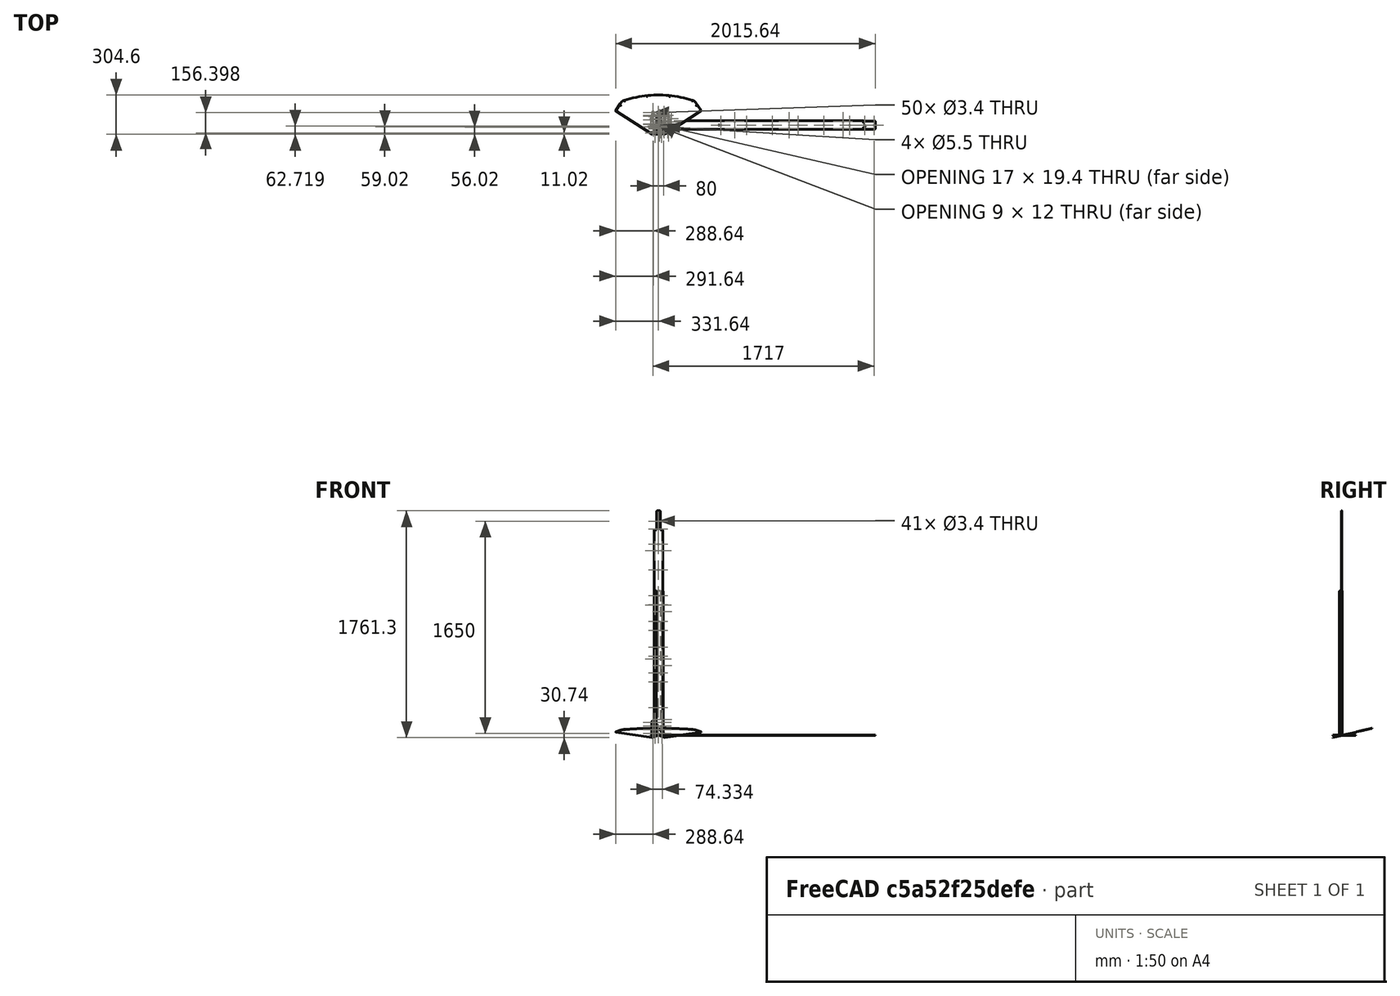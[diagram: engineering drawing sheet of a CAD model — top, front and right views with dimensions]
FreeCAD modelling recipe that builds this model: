
FCSTD DOCUMENT  (FreeCAD 0.21R32532 (Git))
Label: compostit_full_size2part_ss
License: All rights reserved
LicenseURL: http://en.wikipedia.org/wiki/All_rights_reserved
objects: TechDraw::DrawViewDimension×59, Sketcher::SketchObject×27, TechDraw::DrawViewPart×26, TechDraw::DrawPage×11, App::Link×9, Part::Feature×9, App::DocumentObjectGroup×8, Part::Mirroring×3, PartDesign::FeatureBase×1, PartDesign::Body×1, TechDraw::DrawSVGTemplate×1
note: 150 computed .brp shape members not serialized (recipe doc carries the construction recipe); baked Part::Feature solids carry a one-line shape summary decoded from their .brp
EXTERNAL_REF file=composit_full_size2part.FCStd obj=Body029
EXTERNAL_REF file=composit_full_size2part.FCStd obj=Body033
EXTERNAL_REF file=composit_full_size2part.FCStd obj=Body034
EXTERNAL_REF file=composit_full_size2part.FCStd obj=Body058
EXTERNAL_REF file=composit_full_size2part.FCStd obj=cover_bended
EXTERNAL_REF file=composit_full_size2part.FCStd obj=Body065
EXTERNAL_REF file=composit_full_size2part.FCStd obj=Body064
EXTERNAL_REF file=composit_full_size2part.FCStd obj=Body066
EXTERNAL_REF file=composit_full_size2part.FCStd obj=Body067

FEATURE [App::Link] Link  label="pillar"
  LinkedObject = -> <external composit_full_size2part.FCStd>#Body029
  expr: LinkedObject = composit_full_size2part#<<pillar_material_0.45ansi>>._self
FEATURE [App::Link] Link001
  LinkedObject = -> <external composit_full_size2part.FCStd>#Body033
  expr: LinkedObject = composit_full_size2part#<<pillar_corner_top_material_0.40ansi>>._self
FEATURE [App::Link] Link002
  LinkedObject = -> <external composit_full_size2part.FCStd>#Body034
  expr: LinkedObject = composit_full_size2part#<<pillar_corner_bottom_material_0.40ansi>>._self
FEATURE [App::Link] Link003  label="dec_corner_link"
  LinkedObject = -> <external composit_full_size2part.FCStd>#Body058
  expr: LinkedObject = composit_full_size2part#<<dec_corner_material_0.50ansi>>._self
FEATURE [App::Link] Link004
  LinkedObject = -> <external composit_full_size2part.FCStd>#cover_bended
  expr: LinkedObject = composit_full_size2part#<<cover_bended_material_0.45ansi>>._self
FEATURE [Part::Feature] Unfold001
  shape: bbox 28.6 x 144.4 x 2.247 mm, 22 faces (baked)
FEATURE [Sketcher::SketchObject] Unfold_Sketch001
  FullyConstrained = false
  sketch-geometry (20):
    g0: BSplineCurve PolesCount=34 KnotsCount=9 Degree=5 IsPeriodic=0
    g1: LineSegment StartX=-9.3 StartY=74.3982 StartZ=0 EndX=9.3 EndY=74.3982 EndZ=0
    g2: BSplineCurve PolesCount=34 KnotsCount=9 Degree=5 IsPeriodic=0
    g3: LineSegment StartX=-9.3 StartY=-70 StartZ=0 EndX=9.3 EndY=-70 EndZ=0
    g4: BSplineCurve PolesCount=34 KnotsCount=9 Degree=5 IsPeriodic=0
    g5: BSplineCurve PolesCount=34 KnotsCount=9 Degree=5 IsPeriodic=0
    g6: ArcOfCircle CenterX=-3 CenterY=-19.5 CenterZ=0 NormalX=0 NormalY=0 NormalZ=1 AngleXU=0 Radius=1.5 StartAngle=3.14159 EndAngle=4.71239
    g7: LineSegment StartX=-4.5 StartY=-19.5 StartZ=0 EndX=-4.5 EndY=-10.5 EndZ=0
    g8: ArcOfCircle CenterX=-3 CenterY=-10.5 CenterZ=0 NormalX=0 NormalY=0 NormalZ=1 AngleXU=0 Radius=1.5 StartAngle=1.5708 EndAngle=3.14159
    g9: LineSegment StartX=-3 StartY=-9 StartZ=0 EndX=3 EndY=-9 EndZ=0
    g10: ArcOfCircle CenterX=3 CenterY=-10.5 CenterZ=0 NormalX=0 NormalY=0 NormalZ=1 AngleXU=0 Radius=1.5 StartAngle=-1.91e-13 EndAngle=1.5708
    g11: LineSegment StartX=4.5 StartY=-10.5 StartZ=0 EndX=4.5 EndY=-19.5 EndZ=0
    g12: ArcOfCircle CenterX=3 CenterY=-19.5 CenterZ=0 NormalX=0 NormalY=0 NormalZ=1 AngleXU=0 Radius=1.5 StartAngle=4.71239 EndAngle=6.28319
    g13: LineSegment StartX=3 StartY=-21 StartZ=0 EndX=-3 EndY=-21 EndZ=0
    g14: Circle CenterX=3.46e-14 CenterY=66.3982 CenterZ=0 NormalX=0 NormalY=0 NormalZ=1 AngleXU=-5e-16 Radius=1.7
    g15: Circle CenterX=6e-16 CenterY=-60 CenterZ=0 NormalX=0 NormalY=0 NormalZ=1 AngleXU=-3.14159 Radius=1.7
    g16: Circle CenterX=4.6e-15 CenterY=6.39823 CenterZ=0 NormalX=0 NormalY=0 NormalZ=1 AngleXU=-5e-16 Radius=1.7
    g17: Circle CenterX=6e-16 CenterY=-30 CenterZ=0 NormalX=0 NormalY=0 NormalZ=1 AngleXU=-3.14159 Radius=1.7
    g18: LineSegment StartX=-14.3 StartY=69.3982 StartZ=0 EndX=-14.3 EndY=-65 EndZ=0
    g19: LineSegment StartX=14.3 StartY=69.3982 StartZ=0 EndX=14.3 EndY=-65 EndZ=0
FEATURE [Sketcher::SketchObject] Unfold_Sketch_Outline001
  FullyConstrained = false
  sketch-geometry (8):
    g0: BSplineCurve PolesCount=34 KnotsCount=9 Degree=5 IsPeriodic=0
    g1: LineSegment StartX=-9.3 StartY=74.3982 StartZ=0 EndX=9.3 EndY=74.3982 EndZ=0
    g2: BSplineCurve PolesCount=34 KnotsCount=9 Degree=5 IsPeriodic=0
    g3: LineSegment StartX=-14.3 StartY=69.3982 StartZ=0 EndX=-14.3 EndY=-65 EndZ=0
    g4: BSplineCurve PolesCount=34 KnotsCount=9 Degree=5 IsPeriodic=0
    g5: LineSegment StartX=-9.3 StartY=-70 StartZ=0 EndX=9.3 EndY=-70 EndZ=0
    g6: BSplineCurve PolesCount=34 KnotsCount=9 Degree=5 IsPeriodic=0
    g7: LineSegment StartX=14.3 StartY=69.3982 StartZ=0 EndX=14.3 EndY=-65 EndZ=0
FEATURE [Sketcher::SketchObject] Unfold_Sketch_Internal
  FullyConstrained = false
  sketch-geometry (12):
    g0: ArcOfCircle CenterX=-3 CenterY=-19.5 CenterZ=0 NormalX=0 NormalY=0 NormalZ=1 AngleXU=0 Radius=1.5 StartAngle=3.14159 EndAngle=4.71239
    g1: LineSegment StartX=3 StartY=-21 StartZ=0 EndX=-3 EndY=-21 EndZ=0
    g2: ArcOfCircle CenterX=3 CenterY=-19.5 CenterZ=0 NormalX=0 NormalY=0 NormalZ=1 AngleXU=0 Radius=1.5 StartAngle=4.71239 EndAngle=6.28319
    g3: LineSegment StartX=4.5 StartY=-10.5 StartZ=0 EndX=4.5 EndY=-19.5 EndZ=0
    g4: ArcOfCircle CenterX=3 CenterY=-10.5 CenterZ=0 NormalX=0 NormalY=0 NormalZ=1 AngleXU=0 Radius=1.5 StartAngle=-1.91e-13 EndAngle=1.5708
    g5: LineSegment StartX=-3 StartY=-9 StartZ=0 EndX=3 EndY=-9 EndZ=0
    g6: ArcOfCircle CenterX=-3 CenterY=-10.5 CenterZ=0 NormalX=0 NormalY=0 NormalZ=1 AngleXU=0 Radius=1.5 StartAngle=1.5708 EndAngle=3.14159
    g7: LineSegment StartX=-4.5 StartY=-19.5 StartZ=0 EndX=-4.5 EndY=-10.5 EndZ=0
    g8: Circle CenterX=6e-16 CenterY=-60 CenterZ=0 NormalX=0 NormalY=0 NormalZ=1 AngleXU=-3.14159 Radius=1.7
    g9: Circle CenterX=3.46e-14 CenterY=66.3982 CenterZ=0 NormalX=0 NormalY=0 NormalZ=1 AngleXU=-5e-16 Radius=1.7
    g10: Circle CenterX=4.6e-15 CenterY=6.39823 CenterZ=0 NormalX=0 NormalY=0 NormalZ=1 AngleXU=-5e-16 Radius=1.7
    g11: Circle CenterX=6e-16 CenterY=-30 CenterZ=0 NormalX=0 NormalY=0 NormalZ=1 AngleXU=-3.14159 Radius=1.7
FEATURE [Sketcher::SketchObject] Unfold_Sketch_bends001
  FullyConstrained = false
  Placement = pos=(0,-0.25401,0.626835) rot=(1,0,0;0.385004rad)
  sketch-geometry (1):
    g0: LineSegment StartX=14.3 StartY=-1.66905 StartZ=0 EndX=-14.3 EndY=-1.66905 EndZ=0
FEATURE [Part::Feature] Unfold002
  Placement = pos=(0,0,0) rot=(1,0,0;0.115926rad)
  shape: bbox 663.3 x 304.6 x 72.37 mm, 42 faces (baked)
  expr: .Placement.Rotation.Angle = -<<composit_full_size2part>>#<<bend_angle_sketch>>.Constraints.angle
FEATURE [Sketcher::SketchObject] Unfold_Sketch002
  FullyConstrained = false
  sketch-geometry (47):
    g0: ArcOfCircle CenterX=1.08768 CenterY=-0.0209948 CenterZ=0 NormalX=0 NormalY=0 NormalZ=1 AngleXU=-1.5708 Radius=6 StartAngle=2.93378 EndAngle=3.41126
    g1: LineSegment StartX=-0.510793 StartY=5.76216 StartZ=0 EndX=-13.5644 EndY=14.402 EndZ=0
    g2: ArcOfCircle CenterX=-15.8107 CenterY=11.0082 CenterZ=0 NormalX=0 NormalY=0 NormalZ=1 AngleXU=0.986118 Radius=4.06986 StartAngle=-9e-16 EndAngle=1.0472
    g3: ArcOfCircle CenterX=-19.4427 CenterY=18.2927 CenterZ=0 NormalX=0 NormalY=0 NormalZ=1 AngleXU=0.986118 Radius=4.06986 StartAngle=3.30821 EndAngle=4.18879
    g4: LineSegment StartX=-21.095 StartY=14.5734 StartZ=0 EndX=-72.4671 EndY=48.5753 EndZ=0
    g5: ArcOfCircle CenterX=-71.8547 CenterY=49.3658 CenterZ=0 NormalX=0 NormalY=0 NormalZ=1 AngleXU=0.986118 Radius=1 StartAngle=1.5708 EndAngle=3.06709
    g6: LineSegment StartX=-72.6886 StartY=49.9178 StartZ=0 EndX=113.036 EndY=330.522 EndZ=0
    g7: ArcOfCircle CenterX=115.121 CenterY=329.142 CenterZ=0 NormalX=0 NormalY=0 NormalZ=1 AngleXU=0.986118 Radius=2.5 StartAngle=0 EndAngle=1.5708
    g8: LineSegment StartX=116.501 StartY=331.227 StartZ=0 EndX=170.6 EndY=295.42 EndZ=0
    g9: BSplineCurve PolesCount=15 KnotsCount=13 Degree=3 IsPeriodic=0
    g10: BSplineCurve PolesCount=15 KnotsCount=13 Degree=3 IsPeriodic=0
    g11: BSplineCurve PolesCount=15 KnotsCount=13 Degree=3 IsPeriodic=0
    g12: ArcOfCircle CenterX=1.05156 CenterY=-5.68e-14 CenterZ=0 NormalX=0 NormalY=0 NormalZ=1 AngleXU=-1.5708 Radius=6 StartAngle=0.845226 EndAngle=2.29637
    g13: BSplineCurve PolesCount=15 KnotsCount=13 Degree=3 IsPeriodic=0
    g14: BSplineCurve PolesCount=15 KnotsCount=13 Degree=3 IsPeriodic=0
    g15: BSplineCurve PolesCount=15 KnotsCount=13 Degree=3 IsPeriodic=0
    g16: ArcOfCircle CenterX=174.836 CenterY=292.289 CenterZ=0 NormalX=0 NormalY=0 NormalZ=1 AngleXU=1.5708 Radius=1.5 StartAngle=5.72892 EndAngle=6.93163
    g17: ArcOfCircle CenterX=146.678 CenterY=246.798 CenterZ=0 NormalX=0 NormalY=0 NormalZ=1 AngleXU=-1.5708 Radius=55 StartAngle=1.87889 EndAngle=2.58733
    g18: ArcOfCircle CenterX=-628.863 CenterY=0 CenterZ=0 NormalX=0 NormalY=0 NormalZ=1 AngleXU=-1.5708 Radius=868.863 StartAngle=1.2627 EndAngle=1.87889
    g19: ArcOfCircle CenterX=146.678 CenterY=-246.798 CenterZ=0 NormalX=0 NormalY=0 NormalZ=1 AngleXU=-1.5708 Radius=55 StartAngle=0.554262 EndAngle=1.2627
    g20: ArcOfCircle CenterX=174.836 CenterY=-292.289 CenterZ=0 NormalX=0 NormalY=0 NormalZ=1 AngleXU=-1.5708 Radius=1.5 StartAngle=5.63474 EndAngle=6.83745
    g21: LineSegment StartX=116.501 StartY=-331.227 StartZ=0 EndX=170.6 EndY=-295.42 EndZ=0
    g22: ArcOfCircle CenterX=115.121 CenterY=-329.142 CenterZ=0 NormalX=0 NormalY=0 NormalZ=1 AngleXU=-0.986118 Radius=2.5 StartAngle=4.71239 EndAngle=6.28319
    g23: LineSegment StartX=-72.6886 StartY=-49.9178 StartZ=0 EndX=113.036 EndY=-330.522 EndZ=0
    g24: ArcOfCircle CenterX=-71.8547 CenterY=-49.3658 CenterZ=0 NormalX=0 NormalY=0 NormalZ=1 AngleXU=-0.986118 Radius=1 StartAngle=3.21609 EndAngle=4.71239
    g25: LineSegment StartX=-21.095 StartY=-14.5734 StartZ=0 EndX=-72.4671 EndY=-48.5753 EndZ=0
    g26: LineSegment StartX=-0.510793 StartY=-5.76216 StartZ=0 EndX=-13.5644 EndY=-14.402 EndZ=0
    g27: ArcOfCircle CenterX=-15.8107 CenterY=-11.0082 CenterZ=0 NormalX=0 NormalY=0 NormalZ=1 AngleXU=-0.986118 Radius=4.06986 StartAngle=5.23599 EndAngle=6.28319
    g28: ArcOfCircle CenterX=-19.4427 CenterY=-18.2927 CenterZ=0 NormalX=0 NormalY=0 NormalZ=1 AngleXU=-0.986118 Radius=4.06986 StartAngle=2.0944 EndAngle=2.97497
    g29: Circle CenterX=228.876 CenterY=-88.304 CenterZ=0 NormalX=0 NormalY=0 NormalZ=1 AngleXU=-1.5708 Radius=1.7
    g30: Circle CenterX=228.876 CenterY=88.304 CenterZ=0 NormalX=0 NormalY=0 NormalZ=1 AngleXU=1.5708 Radius=1.7
    g31: Circle CenterX=-60.5239 CenterY=57.4259 CenterZ=0 NormalX=0 NormalY=0 NormalZ=1 AngleXU=0.986118 Radius=1.7
    g32: Circle CenterX=-60.5239 CenterY=-57.4259 CenterZ=0 NormalX=0 NormalY=0 NormalZ=1 AngleXU=-0.986118 Radius=1.7
    g33: Circle CenterX=-18.8294 CenterY=29.8293 CenterZ=0 NormalX=0 NormalY=0 NormalZ=1 AngleXU=0.986118 Radius=1.7
    g34: Circle CenterX=-18.8294 CenterY=-29.8293 CenterZ=0 NormalX=0 NormalY=0 NormalZ=1 AngleXU=-0.986118 Radius=1.7
    g35: Circle CenterX=156.271 CenterY=294.381 CenterZ=0 NormalX=0 NormalY=0 NormalZ=1 AngleXU=0.986118 Radius=1.7
    g36: Circle CenterX=193.31 CenterY=-261.294 CenterZ=0 NormalX=0 NormalY=0 NormalZ=1 AngleXU=-1.5708 Radius=1.7
    g37: Circle CenterX=193.31 CenterY=261.294 CenterZ=0 NormalX=0 NormalY=0 NormalZ=1 AngleXU=1.5708 Radius=1.7
    g38: Circle CenterX=156.271 CenterY=-294.381 CenterZ=0 NormalX=0 NormalY=0 NormalZ=1 AngleXU=-0.986118 Radius=1.7
    g39: Circle CenterX=114.576 CenterY=321.977 CenterZ=0 NormalX=0 NormalY=0 NormalZ=1 AngleXU=0.986118 Radius=1.7
    g40: Circle CenterX=114.576 CenterY=-321.977 CenterZ=0 NormalX=0 NormalY=0 NormalZ=1 AngleXU=-0.986118 Radius=1.7
    g41: ArcOfCircle CenterX=1.08768 CenterY=0.0209948 CenterZ=0 NormalX=0 NormalY=0 NormalZ=1 AngleXU=-1.5708 Radius=6 StartAngle=0 EndAngle=0.207814
    g42: ArcOfCircle CenterX=1.08768 CenterY=0.0209948 CenterZ=0 NormalX=0 NormalY=0 NormalZ=1 AngleXU=-1.5708 Radius=6 StartAngle=6.01352 EndAngle=6.28319
    g43: LineSegment StartX=173.93 StartY=-293.484 StartZ=0 EndX=170.6 EndY=-295.42 EndZ=0
    g44: LineSegment StartX=170.6 StartY=295.42 StartZ=0 EndX=173.93 EndY=293.484 EndZ=0
    g45: LineSegment StartX=115.121 StartY=-331.642 StartZ=0 EndX=121.023 EndY=-331.642 EndZ=0
    g46: LineSegment StartX=115.121 StartY=-331.642 StartZ=0 EndX=115.121 EndY=331.592 EndZ=0
  constraints (6):
    c: Block(g7)
    c: Block(g22)
    c: Horizontal(g45)
    c: Tangent(g45,g22) = -1.5708
    c: Vertical(g46)
    c: Distance(g46) = 663.233
FEATURE [Sketcher::SketchObject] Unfold_Sketch_Outline002
  FullyConstrained = false
  sketch-geometry (33):
    g0: BSplineCurve PolesCount=15 KnotsCount=13 Degree=3 IsPeriodic=0
    g1: BSplineCurve PolesCount=15 KnotsCount=13 Degree=3 IsPeriodic=0
    g2: ArcOfCircle CenterX=1.08768 CenterY=-0.0209948 CenterZ=0 NormalX=0 NormalY=0 NormalZ=1 AngleXU=-1.5708 Radius=6 StartAngle=2.93378 EndAngle=3.41126
    g3: LineSegment StartX=-0.510793 StartY=5.76216 StartZ=0 EndX=-13.5644 EndY=14.402 EndZ=0
    g4: ArcOfCircle CenterX=-15.8107 CenterY=11.0082 CenterZ=0 NormalX=0 NormalY=0 NormalZ=1 AngleXU=0.986118 Radius=4.06986 StartAngle=-9e-16 EndAngle=1.0472
    g5: ArcOfCircle CenterX=-19.4427 CenterY=18.2927 CenterZ=0 NormalX=0 NormalY=0 NormalZ=1 AngleXU=0.986118 Radius=4.06986 StartAngle=3.30821 EndAngle=4.18879
    g6: LineSegment StartX=-21.095 StartY=14.5734 StartZ=0 EndX=-72.4671 EndY=48.5753 EndZ=0
    g7: ArcOfCircle CenterX=-71.8547 CenterY=49.3658 CenterZ=0 NormalX=0 NormalY=0 NormalZ=1 AngleXU=0.986118 Radius=1 StartAngle=1.5708 EndAngle=3.06709
    g8: LineSegment StartX=-72.6886 StartY=49.9178 StartZ=0 EndX=113.036 EndY=330.522 EndZ=0
    g9: ArcOfCircle CenterX=115.121 CenterY=329.142 CenterZ=0 NormalX=0 NormalY=0 NormalZ=1 AngleXU=0.986118 Radius=2.5 StartAngle=0 EndAngle=1.5708
    g10: LineSegment StartX=116.501 StartY=331.227 StartZ=0 EndX=170.6 EndY=295.42 EndZ=0
    g11: LineSegment StartX=170.6 StartY=295.42 StartZ=0 EndX=173.93 EndY=293.484 EndZ=0
    g12: ArcOfCircle CenterX=174.836 CenterY=292.289 CenterZ=0 NormalX=0 NormalY=0 NormalZ=1 AngleXU=1.5708 Radius=1.5 StartAngle=5.72892 EndAngle=6.93163
    g13: ArcOfCircle CenterX=146.678 CenterY=246.798 CenterZ=0 NormalX=0 NormalY=0 NormalZ=1 AngleXU=-1.5708 Radius=55 StartAngle=1.87889 EndAngle=2.58733
    g14: ArcOfCircle CenterX=-628.863 CenterY=0 CenterZ=0 NormalX=0 NormalY=0 NormalZ=1 AngleXU=-1.5708 Radius=868.863 StartAngle=1.2627 EndAngle=1.87889
    g15: ArcOfCircle CenterX=146.678 CenterY=-246.798 CenterZ=0 NormalX=0 NormalY=0 NormalZ=1 AngleXU=-1.5708 Radius=55 StartAngle=0.554262 EndAngle=1.2627
    g16: ArcOfCircle CenterX=174.836 CenterY=-292.289 CenterZ=0 NormalX=0 NormalY=0 NormalZ=1 AngleXU=-1.5708 Radius=1.5 StartAngle=5.63474 EndAngle=6.83745
    g17: LineSegment StartX=173.93 StartY=-293.484 StartZ=0 EndX=170.6 EndY=-295.42 EndZ=0
    g18: LineSegment StartX=116.501 StartY=-331.227 StartZ=0 EndX=170.6 EndY=-295.42 EndZ=0
    g19: ArcOfCircle CenterX=115.121 CenterY=-329.142 CenterZ=0 NormalX=0 NormalY=0 NormalZ=1 AngleXU=-0.986118 Radius=2.5 StartAngle=4.71239 EndAngle=6.28319
    g20: LineSegment StartX=-72.6886 StartY=-49.9178 StartZ=0 EndX=113.036 EndY=-330.522 EndZ=0
    g21: ArcOfCircle CenterX=-71.8547 CenterY=-49.3658 CenterZ=0 NormalX=0 NormalY=0 NormalZ=1 AngleXU=-0.986118 Radius=1 StartAngle=3.21609 EndAngle=4.71239
    g22: LineSegment StartX=-21.095 StartY=-14.5734 StartZ=0 EndX=-72.4671 EndY=-48.5753 EndZ=0
    g23: ArcOfCircle CenterX=-19.4427 CenterY=-18.2927 CenterZ=0 NormalX=0 NormalY=0 NormalZ=1 AngleXU=-0.986118 Radius=4.06986 StartAngle=2.0944 EndAngle=2.97497
    g24: ArcOfCircle CenterX=-15.8107 CenterY=-11.0082 CenterZ=0 NormalX=0 NormalY=0 NormalZ=1 AngleXU=-0.986118 Radius=4.06986 StartAngle=5.23599 EndAngle=6.28319
    g25: LineSegment StartX=-0.510793 StartY=-5.76216 StartZ=0 EndX=-13.5644 EndY=-14.402 EndZ=0
    g26: ArcOfCircle CenterX=1.08768 CenterY=0.0209948 CenterZ=0 NormalX=0 NormalY=0 NormalZ=1 AngleXU=-1.5708 Radius=6 StartAngle=6.01352 EndAngle=6.28319
    g27: ArcOfCircle CenterX=1.08768 CenterY=0.0209948 CenterZ=0 NormalX=0 NormalY=0 NormalZ=1 AngleXU=-1.5708 Radius=6 StartAngle=0 EndAngle=0.207814
    g28: BSplineCurve PolesCount=15 KnotsCount=13 Degree=3 IsPeriodic=0
    g29: BSplineCurve PolesCount=15 KnotsCount=13 Degree=3 IsPeriodic=0
    g30: BSplineCurve PolesCount=15 KnotsCount=13 Degree=3 IsPeriodic=0
    g31: ArcOfCircle CenterX=1.05156 CenterY=-5.68e-14 CenterZ=0 NormalX=0 NormalY=0 NormalZ=1 AngleXU=-1.5708 Radius=6 StartAngle=0.845226 EndAngle=2.29637
    g32: BSplineCurve PolesCount=15 KnotsCount=13 Degree=3 IsPeriodic=0
FEATURE [Sketcher::SketchObject] Unfold_Sketch_Internal001
  FullyConstrained = false
  sketch-geometry (12):
    g0: Circle CenterX=156.271 CenterY=-294.381 CenterZ=0 NormalX=0 NormalY=0 NormalZ=1 AngleXU=-0.986118 Radius=1.7
    g1: Circle CenterX=156.271 CenterY=294.381 CenterZ=0 NormalX=0 NormalY=0 NormalZ=1 AngleXU=0.986118 Radius=1.7
    g2: Circle CenterX=114.576 CenterY=-321.977 CenterZ=0 NormalX=0 NormalY=0 NormalZ=1 AngleXU=-0.986118 Radius=1.7
    g3: Circle CenterX=114.576 CenterY=321.977 CenterZ=0 NormalX=0 NormalY=0 NormalZ=1 AngleXU=0.986118 Radius=1.7
    g4: Circle CenterX=-18.8294 CenterY=-29.8293 CenterZ=0 NormalX=0 NormalY=0 NormalZ=1 AngleXU=-0.986118 Radius=1.7
    g5: Circle CenterX=-18.8294 CenterY=29.8293 CenterZ=0 NormalX=0 NormalY=0 NormalZ=1 AngleXU=0.986118 Radius=1.7
    g6: Circle CenterX=-60.5239 CenterY=-57.4259 CenterZ=0 NormalX=0 NormalY=0 NormalZ=1 AngleXU=-0.986118 Radius=1.7
    g7: Circle CenterX=-60.5239 CenterY=57.4259 CenterZ=0 NormalX=0 NormalY=0 NormalZ=1 AngleXU=0.986118 Radius=1.7
    g8: Circle CenterX=228.876 CenterY=88.304 CenterZ=0 NormalX=0 NormalY=0 NormalZ=1 AngleXU=1.5708 Radius=1.7
    g9: Circle CenterX=228.876 CenterY=-88.304 CenterZ=0 NormalX=0 NormalY=0 NormalZ=1 AngleXU=-1.5708 Radius=1.7
    g10: Circle CenterX=193.31 CenterY=261.294 CenterZ=0 NormalX=0 NormalY=0 NormalZ=1 AngleXU=1.5708 Radius=1.7
    g11: Circle CenterX=193.31 CenterY=-261.294 CenterZ=0 NormalX=0 NormalY=0 NormalZ=1 AngleXU=-1.5708 Radius=1.7
FEATURE [Sketcher::SketchObject] Unfold_Sketch_bends002
  FullyConstrained = false
  sketch-geometry (2):
    g0: LineSegment StartX=4.08479 StartY=5.17687 StartZ=0 EndX=172.236 EndY=294.469 EndZ=0
    g1: LineSegment StartX=4.08479 StartY=-5.17687 StartZ=0 EndX=172.236 EndY=-294.469 EndZ=0
FEATURE [TechDraw::DrawViewPart] View
  CoarseView = false
  Direction = (0,0,1)
  Focus = 100
  HardHidden = false
  IsoCount = 0
  IsoHidden = false
  IsoVisible = false
  LockPosition = false
  Perspective = false
  Rotation = 0
  Scale = 0.3
  ScaleType = 2
  SeamHidden = false
  SeamVisible = true
  SmoothHidden = false
  SmoothVisible = true
  X = 205.5
  XDirection = (1,-2.98023e-07,0)
  XSource = -> [Link004]
  Y = 169.202
FEATURE [TechDraw::DrawViewPart] View002
  CoarseView = false
  Direction = (-0.5,-0.866025,0)
  Focus = 100
  HardHidden = false
  IsoCount = 0
  IsoHidden = false
  IsoVisible = false
  LockPosition = false
  Perspective = false
  Rotation = 0
  Scale = 0.5
  ScaleType = 2
  SeamHidden = false
  SeamVisible = true
  SmoothHidden = false
  SmoothVisible = true
  X = 155.605
  XDirection = (0.866025,-0.5,-5.9605e-08)
  XSource = -> [Link004]
  Y = 37.8553
FEATURE [TechDraw::DrawViewDimension] Dimension
  AngleOverride = false
  Arbitrary = false
  ArbitraryTolerances = false
  EqualTolerance = true
  ExtensionAngle = 0
  FormatSpec = %.2w
  FormatSpecOverTolerance = %+.2w
  FormatSpecUnderTolerance = %+.2w
  Inverted = false
  LineAngle = 0
  LockPosition = false
  MeasureType = 1
  OverTolerance = 0
  References2D = -> [View]
  Rotation = 0
  ScaleType = 0
  TheoreticalExact = false
  Type = 0
  UnderTolerance = 0
  X = -36.5372
  Y = -2.03391
FEATURE [TechDraw::DrawViewDimension] Dimension001
  AngleOverride = false
  Arbitrary = false
  ArbitraryTolerances = false
  EqualTolerance = true
  ExtensionAngle = 0
  FormatSpec = %.2w
  FormatSpecOverTolerance = %+.2w
  FormatSpecUnderTolerance = %+.2w
  Inverted = false
  LineAngle = 0
  LockPosition = false
  MeasureType = 1
  OverTolerance = 0
  References2D = -> [View]
  Rotation = 0
  ScaleType = 0
  TheoreticalExact = false
  Type = 6
  UnderTolerance = 0
  X = 2.75033
  Y = -10.9437
FEATURE [TechDraw::DrawViewDimension] Dimension003
  AngleOverride = false
  Arbitrary = false
  ArbitraryTolerances = false
  EqualTolerance = true
  ExtensionAngle = 0
  FormatSpec = %.2w
  FormatSpecOverTolerance = %+.2w
  FormatSpecUnderTolerance = %+.2w
  Inverted = false
  LineAngle = 0
  LockPosition = false
  MeasureType = 1
  OverTolerance = 0
  References2D = -> [View002]
  Rotation = 0
  ScaleType = 0
  TheoreticalExact = false
  Type = 2
  UnderTolerance = 0
  X = 53.4792
  Y = 2.41455
FEATURE [TechDraw::DrawViewDimension] Dimension004
  AngleOverride = false
  Arbitrary = false
  ArbitraryTolerances = false
  EqualTolerance = true
  ExtensionAngle = 0
  FormatSpec = %.2w
  FormatSpecOverTolerance = %+.2w
  FormatSpecUnderTolerance = %+.2w
  Inverted = false
  LineAngle = 0
  LockPosition = false
  MeasureType = 1
  OverTolerance = 0
  References2D = -> [View002]
  Rotation = 0
  ScaleType = 0
  TheoreticalExact = false
  Type = 2
  UnderTolerance = 0
  X = -140.691
  Y = 10.1583
FEATURE [TechDraw::DrawViewPart] View003
  CoarseView = false
  Direction = (-0.864561,0.499155,0.0581257)
  Focus = 100
  HardHidden = false
  IsoCount = 0
  IsoHidden = false
  IsoVisible = false
  LockPosition = false
  Perspective = false
  Rotation = 0
  Scale = 0.5
  ScaleType = 2
  SeamHidden = false
  SeamVisible = true
  SmoothHidden = false
  SmoothVisible = true
  X = 88.1252
  XDirection = (-0.5,-0.866025,9.992e-08)
  XSource = -> [Link004]
  Y = 113.254
FEATURE [TechDraw::DrawViewDimension] Dimension005
  AngleOverride = false
  Arbitrary = false
  ArbitraryTolerances = false
  EqualTolerance = true
  ExtensionAngle = 0
  FormatSpec = %.2w
  FormatSpecOverTolerance = %+.2w
  FormatSpecUnderTolerance = %+.2w
  Inverted = false
  LineAngle = 0
  LockPosition = false
  MeasureType = 1
  OverTolerance = 0
  References2D = -> [View003]
  Rotation = 0
  ScaleType = 0
  TheoreticalExact = false
  Type = 6
  UnderTolerance = 0
  X = 47.3154
  Y = 1.62344
FEATURE [TechDraw::DrawViewDimension] Dimension006
  AngleOverride = false
  Arbitrary = false
  ArbitraryTolerances = false
  EqualTolerance = true
  ExtensionAngle = 0
  FormatSpec = R%.2w
  FormatSpecOverTolerance = %+.2w
  FormatSpecUnderTolerance = %+.2w
  Inverted = false
  LineAngle = 0
  LockPosition = false
  MeasureType = 1
  OverTolerance = 0
  References2D = -> [View003]
  Rotation = 0
  ScaleType = 0
  TheoreticalExact = false
  Type = 4
  UnderTolerance = 0
  X = 56.0146
  Y = -10.3945
FEATURE [TechDraw::DrawViewDimension] Dimension007
  AngleOverride = false
  Arbitrary = false
  ArbitraryTolerances = false
  EqualTolerance = true
  ExtensionAngle = 0
  FormatSpec = %.2w
  FormatSpecOverTolerance = %+.2w
  FormatSpecUnderTolerance = %+.2w
  Inverted = false
  LineAngle = 0
  LockPosition = false
  MeasureType = 1
  OverTolerance = 0
  References2D = -> [View003]
  Rotation = 0
  ScaleType = 0
  TheoreticalExact = false
  Type = 2
  UnderTolerance = 0
  X = 84.4025
  Y = -2.10043
FEATURE [TechDraw::DrawViewPart] View004
  CoarseView = false
  Direction = (-8.7423e-08,1,0)
  Focus = 100
  HardHidden = false
  IsoCount = 0
  IsoHidden = false
  IsoVisible = false
  LockPosition = false
  Perspective = false
  Rotation = 90
  Scale = 0.17
  ScaleType = 2
  SeamHidden = false
  SeamVisible = true
  SmoothHidden = false
  SmoothVisible = true
  X = 148.5
  XDirection = (-1,-8.7423e-08,0)
  XSource = -> [Link]
  Y = 191.322
  expr: X = Template.Width / 2
FEATURE [TechDraw::DrawViewPart] View005
  CoarseView = false
  Direction = (1,-2.9802e-08,2.9802e-08)
  Focus = 100
  HardHidden = false
  IsoCount = 0
  IsoHidden = false
  IsoVisible = false
  LockPosition = false
  Perspective = false
  Rotation = 90
  Scale = 0.17
  ScaleType = 2
  SeamHidden = false
  SeamVisible = true
  SmoothHidden = false
  SmoothVisible = true
  X = 148.5
  XDirection = (2.9802e-08,1,-2.38419e-07)
  XSource = -> [Link]
  Y = 126.779
  expr: X = Template.Width / 2
FEATURE [TechDraw::DrawViewPart] View006
  CoarseView = false
  Direction = (0,0,1)
  Focus = 100
  HardHidden = false
  IsoCount = 0
  IsoHidden = false
  IsoVisible = false
  LockPosition = false
  Perspective = false
  Rotation = 90
  ScaleType = 0
  SeamHidden = false
  SeamVisible = true
  SmoothHidden = false
  SmoothVisible = true
  X = 62.8986
  XDirection = (1,-1.19209e-07,0)
  XSource = -> [Link]
  Y = 46.3276
FEATURE [TechDraw::DrawViewDimension] Dimension008
  AngleOverride = false
  Arbitrary = false
  ArbitraryTolerances = false
  EqualTolerance = true
  ExtensionAngle = 0
  FormatSpec = %.2w
  FormatSpecOverTolerance = %+.2w
  FormatSpecUnderTolerance = %+.2w
  Inverted = false
  LineAngle = 0
  LockPosition = false
  MeasureType = 1
  OverTolerance = 0
  References2D = -> [View004]
  Rotation = 0
  ScaleType = 0
  TheoreticalExact = false
  Type = 2
  UnderTolerance = 0
  X = -139.864
  Y = -8.5074
FEATURE [TechDraw::DrawViewDimension] Dimension009
  AngleOverride = false
  Arbitrary = false
  ArbitraryTolerances = false
  EqualTolerance = true
  ExtensionAngle = 0
  FormatSpec = %.2w
  FormatSpecOverTolerance = %+.2w
  FormatSpecUnderTolerance = %+.2w
  Inverted = false
  LineAngle = 0
  LockPosition = false
  MeasureType = 1
  OverTolerance = 0
  References2D = -> [View004]
  Rotation = 0
  ScaleType = 0
  TheoreticalExact = false
  Type = 2
  UnderTolerance = 0
  X = 139.408
  Y = -10.9738
FEATURE [TechDraw::DrawViewDimension] Dimension010
  AngleOverride = false
  Arbitrary = false
  ArbitraryTolerances = false
  EqualTolerance = true
  ExtensionAngle = 0
  FormatSpec = %.2w
  FormatSpecOverTolerance = %+.2w
  FormatSpecUnderTolerance = %+.2w
  Inverted = false
  LineAngle = 0
  LockPosition = false
  MeasureType = 1
  OverTolerance = 0
  References2D = -> [View005]
  Rotation = 0
  ScaleType = 0
  TheoreticalExact = false
  Type = 2
  UnderTolerance = 0
  X = -139.272
  Y = -6.78963
FEATURE [TechDraw::DrawViewDimension] Dimension011
  AngleOverride = false
  Arbitrary = false
  ArbitraryTolerances = false
  EqualTolerance = true
  ExtensionAngle = 0
  FormatSpec = %.2w
  FormatSpecOverTolerance = %+.2w
  FormatSpecUnderTolerance = %+.2w
  Inverted = false
  LineAngle = 0
  LockPosition = false
  MeasureType = 1
  OverTolerance = 0
  References2D = -> [View005]
  Rotation = 0
  ScaleType = 0
  TheoreticalExact = false
  Type = 2
  UnderTolerance = 0
  X = 137.656
  Y = -2.54713
FEATURE [TechDraw::DrawViewDimension] Dimension012
  AngleOverride = false
  Arbitrary = false
  ArbitraryTolerances = false
  EqualTolerance = true
  ExtensionAngle = 0
  FormatSpec = %.2w
  FormatSpecOverTolerance = %+.2w
  FormatSpecUnderTolerance = %+.2w
  Inverted = false
  LineAngle = 0
  LockPosition = false
  MeasureType = 1
  OverTolerance = 0
  References2D = -> [View006]
  Rotation = 0
  ScaleType = 0
  TheoreticalExact = false
  Type = 1
  UnderTolerance = 0
  X = -2.45845
  Y = 40.9333
FEATURE [TechDraw::DrawViewDimension] Dimension013
  AngleOverride = false
  Arbitrary = false
  ArbitraryTolerances = false
  EqualTolerance = true
  ExtensionAngle = 0
  FormatSpec = R%.2w
  FormatSpecOverTolerance = %+.2w
  FormatSpecUnderTolerance = %+.2w
  Inverted = false
  LineAngle = 0
  LockPosition = false
  MeasureType = 1
  OverTolerance = 0
  References2D = -> [View005]
  Rotation = 0
  ScaleType = 0
  TheoreticalExact = false
  Type = 4
  UnderTolerance = 0
  X = -137.844
  Y = 28.2706
FEATURE [TechDraw::DrawViewDimension] Dimension014
  AngleOverride = false
  Arbitrary = false
  ArbitraryTolerances = false
  EqualTolerance = true
  ExtensionAngle = 0
  FormatSpec = R%.2w
  FormatSpecOverTolerance = %+.2w
  FormatSpecUnderTolerance = %+.2w
  Inverted = false
  LineAngle = 0
  LockPosition = false
  MeasureType = 1
  OverTolerance = 0
  References2D = -> [View006]
  Rotation = 0
  ScaleType = 0
  TheoreticalExact = false
  Type = 4
  UnderTolerance = 0
  X = -22.5253
  Y = -5.539
FEATURE [TechDraw::DrawViewDimension] Dimension015
  AngleOverride = false
  Arbitrary = false
  ArbitraryTolerances = false
  EqualTolerance = true
  ExtensionAngle = 0
  FormatSpec = %.2w
  FormatSpecOverTolerance = %+.2w
  FormatSpecUnderTolerance = %+.2w
  Inverted = false
  LineAngle = 0
  LockPosition = false
  MeasureType = 1
  OverTolerance = 0
  References2D = -> [View006]
  Rotation = 0
  ScaleType = 0
  TheoreticalExact = false
  Type = 2
  UnderTolerance = 0
  X = -47.4026
  Y = 1.02293
FEATURE [TechDraw::DrawViewDimension] Dimension016
  AngleOverride = false
  Arbitrary = false
  ArbitraryTolerances = false
  EqualTolerance = true
  ExtensionAngle = 0
  FormatSpec = %.2w
  FormatSpecOverTolerance = %+.2w
  FormatSpecUnderTolerance = %+.2w
  Inverted = false
  LineAngle = 0
  LockPosition = false
  MeasureType = 1
  OverTolerance = 0
  References2D = -> [View006]
  Rotation = 0
  ScaleType = 0
  TheoreticalExact = false
  Type = 2
  UnderTolerance = 0
  X = 53.0082
  Y = 4.90023
FEATURE [Part::Feature] Unfold004
  shape: bbox 67.71 x 2.245 x 1745 mm, 38 faces (baked)
FEATURE [Sketcher::SketchObject] Unfold_Sketch004
  FullyConstrained = false
  sketch-geometry (36):
    g0: BSplineCurve PolesCount=34 KnotsCount=9 Degree=5 IsPeriodic=0
    g1: LineSegment StartX=5 StartY=-33.8553 StartZ=0 EndX=1591 EndY=-33.8553 EndZ=0
    g2: BSplineCurve PolesCount=34 KnotsCount=9 Degree=5 IsPeriodic=0
    g3: LineSegment StartX=1596 StartY=-28.8553 StartZ=0 EndX=1596 EndY=-14.3 EndZ=0
    g4: LineSegment StartX=1596 StartY=-14.3 StartZ=0 EndX=1739.56 EndY=-14.3 EndZ=0
    g5: ArcOfCircle CenterX=1739.56 CenterY=-9.3 CenterZ=0 NormalX=0 NormalY=0 NormalZ=1 AngleXU=-1.5708 Radius=5 StartAngle=0 EndAngle=1.5708
    g6: LineSegment StartX=1744.56 StartY=-9.3 StartZ=0 EndX=1744.56 EndY=9.3 EndZ=0
    g7: ArcOfCircle CenterX=1739.56 CenterY=9.3 CenterZ=0 NormalX=0 NormalY=0 NormalZ=1 AngleXU=1.5708 Radius=5 StartAngle=4.71239 EndAngle=6.28319
    g8: LineSegment StartX=1739.56 StartY=14.3 StartZ=0 EndX=1596 EndY=14.3 EndZ=0
    g9: LineSegment StartX=1596 StartY=14.3 StartZ=0 EndX=1596 EndY=28.8553 EndZ=0
    g10: BSplineCurve PolesCount=34 KnotsCount=9 Degree=5 IsPeriodic=0
    g11: LineSegment StartX=5 StartY=33.8553 StartZ=0 EndX=1591 EndY=33.8553 EndZ=0
    g12: BSplineCurve PolesCount=34 KnotsCount=9 Degree=5 IsPeriodic=0
    g13: LineSegment StartX=0 StartY=-28.8553 StartZ=0 EndX=0 EndY=28.8553 EndZ=0
    g14: Circle CenterX=1434 CenterY=-26.8553 CenterZ=0 NormalX=0 NormalY=0 NormalZ=-1 AngleXU=1.5708 Radius=1.7
    g15: Circle CenterX=1434 CenterY=26.8553 CenterZ=0 NormalX=0 NormalY=0 NormalZ=1 AngleXU=-1.5708 Radius=1.7
    g16: Circle CenterX=594 CenterY=26.8553 CenterZ=0 NormalX=0 NormalY=0 NormalZ=1 AngleXU=-1.5708 Radius=1.7
    g17: Circle CenterX=1014 CenterY=26.8553 CenterZ=0 NormalX=0 NormalY=0 NormalZ=1 AngleXU=-1.5708 Radius=1.7
    g18: Circle CenterX=1014 CenterY=-26.8553 CenterZ=0 NormalX=0 NormalY=0 NormalZ=-1 AngleXU=1.5708 Radius=1.7
    g19: Circle CenterX=594 CenterY=-26.8553 CenterZ=0 NormalX=0 NormalY=0 NormalZ=-1 AngleXU=1.5708 Radius=1.7
    g20: Circle CenterX=1604 CenterY=0 CenterZ=0 NormalX=0 NormalY=0 NormalZ=1 AngleXU=1.5708 Radius=1.7
    g21: Circle CenterX=1664 CenterY=0 CenterZ=0 NormalX=0 NormalY=0 NormalZ=1 AngleXU=1.5708 Radius=1.7
    g22: Circle CenterX=1486 CenterY=0 CenterZ=0 NormalX=0 NormalY=0 NormalZ=1 AngleXU=1.5708 Radius=1.7
    g23: Circle CenterX=1286 CenterY=0 CenterZ=0 NormalX=0 NormalY=0 NormalZ=1 AngleXU=1.5708 Radius=1.7
    g24: Circle CenterX=1086 CenterY=0 CenterZ=0 NormalX=0 NormalY=0 NormalZ=1 AngleXU=1.5708 Radius=1.7
    g25: Circle CenterX=886 CenterY=0 CenterZ=0 NormalX=0 NormalY=0 NormalZ=1 AngleXU=1.5708 Radius=1.7
    g26: Circle CenterX=686 CenterY=0 CenterZ=0 NormalX=0 NormalY=0 NormalZ=1 AngleXU=1.5708 Radius=1.7
    g27: Circle CenterX=71.3333 CenterY=-26.3553 CenterZ=0 NormalX=0 NormalY=0 NormalZ=1 AngleXU=-3.14159 Radius=1.7
    g28: Circle CenterX=100 CenterY=-26.3553 CenterZ=0 NormalX=0 NormalY=0 NormalZ=1 AngleXU=-3.14159 Radius=1.7
    g29: Circle CenterX=100 CenterY=26.3553 CenterZ=0 NormalX=0 NormalY=0 NormalZ=1 AngleXU=-3.14159 Radius=1.7
    g30: Circle CenterX=71.3333 CenterY=26.3553 CenterZ=0 NormalX=0 NormalY=0 NormalZ=1 AngleXU=-3.14159 Radius=1.7
    g31: Circle CenterX=42.6667 CenterY=26.3553 CenterZ=0 NormalX=0 NormalY=0 NormalZ=1 AngleXU=-3.14159 Radius=1.7
    g32: Circle CenterX=42.6667 CenterY=-26.3553 CenterZ=0 NormalX=0 NormalY=0 NormalZ=1 AngleXU=-3.14159 Radius=1.7
    g33: Circle CenterX=14 CenterY=-26.3553 CenterZ=0 NormalX=0 NormalY=0 NormalZ=1 AngleXU=-3.14159 Radius=1.7
    g34: Circle CenterX=14 CenterY=26.3553 CenterZ=0 NormalX=0 NormalY=0 NormalZ=1 AngleXU=-3.14159 Radius=1.7
    g35: Circle CenterX=486 CenterY=0 CenterZ=0 NormalX=0 NormalY=0 NormalZ=1 AngleXU=1.5708 Radius=1.7
FEATURE [Sketcher::SketchObject] Unfold_Sketch_Outline004
  FullyConstrained = false
  sketch-geometry (14):
    g0: BSplineCurve PolesCount=34 KnotsCount=9 Degree=5 IsPeriodic=0
    g1: LineSegment StartX=5 StartY=-33.8553 StartZ=0 EndX=1591 EndY=-33.8553 EndZ=0
    g2: BSplineCurve PolesCount=34 KnotsCount=9 Degree=5 IsPeriodic=0
    g3: LineSegment StartX=1596 StartY=-28.8553 StartZ=0 EndX=1596 EndY=-14.3 EndZ=0
    g4: LineSegment StartX=1596 StartY=-14.3 StartZ=0 EndX=1739.56 EndY=-14.3 EndZ=0
    g5: ArcOfCircle CenterX=1739.56 CenterY=-9.3 CenterZ=0 NormalX=0 NormalY=0 NormalZ=1 AngleXU=-1.5708 Radius=5 StartAngle=0 EndAngle=1.5708
    g6: LineSegment StartX=1744.56 StartY=-9.3 StartZ=0 EndX=1744.56 EndY=9.3 EndZ=0
    g7: ArcOfCircle CenterX=1739.56 CenterY=9.3 CenterZ=0 NormalX=0 NormalY=0 NormalZ=1 AngleXU=1.5708 Radius=5 StartAngle=4.71239 EndAngle=6.28319
    g8: LineSegment StartX=1739.56 StartY=14.3 StartZ=0 EndX=1596 EndY=14.3 EndZ=0
    g9: LineSegment StartX=1596 StartY=14.3 StartZ=0 EndX=1596 EndY=28.8553 EndZ=0
    g10: BSplineCurve PolesCount=34 KnotsCount=9 Degree=5 IsPeriodic=0
    g11: LineSegment StartX=5 StartY=33.8553 StartZ=0 EndX=1591 EndY=33.8553 EndZ=0
    g12: BSplineCurve PolesCount=34 KnotsCount=9 Degree=5 IsPeriodic=0
    g13: LineSegment StartX=0 StartY=-28.8553 StartZ=0 EndX=0 EndY=28.8553 EndZ=0
FEATURE [Sketcher::SketchObject] Unfold_Sketch_Internal003
  FullyConstrained = false
  sketch-geometry (22):
    g0: Circle CenterX=594 CenterY=-26.8553 CenterZ=0 NormalX=0 NormalY=0 NormalZ=-1 AngleXU=1.5708 Radius=1.7
    g1: Circle CenterX=1014 CenterY=-26.8553 CenterZ=0 NormalX=0 NormalY=0 NormalZ=-1 AngleXU=1.5708 Radius=1.7
    g2: Circle CenterX=1014 CenterY=26.8553 CenterZ=0 NormalX=0 NormalY=0 NormalZ=1 AngleXU=-1.5708 Radius=1.7
    g3: Circle CenterX=594 CenterY=26.8553 CenterZ=0 NormalX=0 NormalY=0 NormalZ=1 AngleXU=-1.5708 Radius=1.7
    g4: Circle CenterX=1434 CenterY=26.8553 CenterZ=0 NormalX=0 NormalY=0 NormalZ=1 AngleXU=-1.5708 Radius=1.7
    g5: Circle CenterX=1434 CenterY=-26.8553 CenterZ=0 NormalX=0 NormalY=0 NormalZ=-1 AngleXU=1.5708 Radius=1.7
    g6: Circle CenterX=486 CenterY=0 CenterZ=0 NormalX=0 NormalY=0 NormalZ=1 AngleXU=1.5708 Radius=1.7
    g7: Circle CenterX=42.6667 CenterY=-26.3553 CenterZ=0 NormalX=0 NormalY=0 NormalZ=1 AngleXU=-3.14159 Radius=1.7
    g8: Circle CenterX=42.6667 CenterY=26.3553 CenterZ=0 NormalX=0 NormalY=0 NormalZ=1 AngleXU=-3.14159 Radius=1.7
    g9: Circle CenterX=71.3333 CenterY=26.3553 CenterZ=0 NormalX=0 NormalY=0 NormalZ=1 AngleXU=-3.14159 Radius=1.7
    g10: Circle CenterX=100 CenterY=26.3553 CenterZ=0 NormalX=0 NormalY=0 NormalZ=1 AngleXU=-3.14159 Radius=1.7
    g11: Circle CenterX=100 CenterY=-26.3553 CenterZ=0 NormalX=0 NormalY=0 NormalZ=1 AngleXU=-3.14159 Radius=1.7
    g12: Circle CenterX=71.3333 CenterY=-26.3553 CenterZ=0 NormalX=0 NormalY=0 NormalZ=1 AngleXU=-3.14159 Radius=1.7
    g13: Circle CenterX=14 CenterY=26.3553 CenterZ=0 NormalX=0 NormalY=0 NormalZ=1 AngleXU=-3.14159 Radius=1.7
    g14: Circle CenterX=14 CenterY=-26.3553 CenterZ=0 NormalX=0 NormalY=0 NormalZ=1 AngleXU=-3.14159 Radius=1.7
    g15: Circle CenterX=686 CenterY=0 CenterZ=0 NormalX=0 NormalY=0 NormalZ=1 AngleXU=1.5708 Radius=1.7
    g16: Circle CenterX=886 CenterY=0 CenterZ=0 NormalX=0 NormalY=0 NormalZ=1 AngleXU=1.5708 Radius=1.7
    g17: Circle CenterX=1086 CenterY=0 CenterZ=0 NormalX=0 NormalY=0 NormalZ=1 AngleXU=1.5708 Radius=1.7
    g18: Circle CenterX=1286 CenterY=0 CenterZ=0 NormalX=0 NormalY=0 NormalZ=1 AngleXU=1.5708 Radius=1.7
    g19: Circle CenterX=1486 CenterY=0 CenterZ=0 NormalX=0 NormalY=0 NormalZ=1 AngleXU=1.5708 Radius=1.7
    g20: Circle CenterX=1664 CenterY=0 CenterZ=0 NormalX=0 NormalY=0 NormalZ=1 AngleXU=1.5708 Radius=1.7
    g21: Circle CenterX=1604 CenterY=0 CenterZ=0 NormalX=0 NormalY=0 NormalZ=1 AngleXU=1.5708 Radius=1.7
FEATURE [Sketcher::SketchObject] Unfold_Sketch_bends004
  FullyConstrained = false
  sketch-geometry (3):
    g0: LineSegment StartX=1596 StartY=-16.5777 StartZ=0 EndX=0 EndY=-16.5777 EndZ=0
    g1: LineSegment StartX=1596 StartY=16.5777 StartZ=0 EndX=0 EndY=16.5777 EndZ=0
    g2: LineSegment StartX=1676.28 StartY=14.3 StartZ=0 EndX=1676.28 EndY=-14.3 EndZ=0
FEATURE [TechDraw::DrawViewPart] View010
  CoarseView = false
  Direction = (0,-1,0)
  Focus = 100
  HardHidden = false
  IsoCount = 0
  IsoHidden = false
  IsoVisible = false
  LockPosition = false
  Perspective = false
  Rotation = 0
  ScaleType = 0
  SeamHidden = false
  SeamVisible = true
  SmoothHidden = false
  SmoothVisible = true
  X = 232.648
  XDirection = (1,0,0)
  XSource = -> [Link001]
  Y = 101.626
FEATURE [TechDraw::DrawViewPart] View011
  CoarseView = false
  Direction = (1,-3.8743e-07,2.68221e-07)
  Focus = 100
  HardHidden = false
  IsoCount = 0
  IsoHidden = false
  IsoVisible = false
  LockPosition = false
  Perspective = false
  Rotation = 0
  ScaleType = 0
  SeamHidden = false
  SeamVisible = true
  SmoothHidden = false
  SmoothVisible = true
  X = 49.5896
  XDirection = (3.8743e-07,1,-3.57628e-07)
  XSource = -> [Link001]
  Y = 103.155
FEATURE [TechDraw::DrawViewPart] View012
  CoarseView = false
  Direction = (-3.58248e-07,4.71724e-07,1)
  Focus = 100
  HardHidden = false
  IsoCount = 0
  IsoHidden = false
  IsoVisible = false
  LockPosition = false
  Perspective = false
  Rotation = 0
  ScaleType = 0
  SeamHidden = false
  SeamVisible = true
  SmoothHidden = false
  SmoothVisible = true
  X = 148.5
  XDirection = (1,-5.36442e-07,3.58248e-07)
  XSource = -> [Link001]
  Y = 97.9316
FEATURE [TechDraw::DrawViewDimension] Dimension023
  AngleOverride = false
  Arbitrary = false
  ArbitraryTolerances = false
  EqualTolerance = true
  ExtensionAngle = 0
  FormatSpec = %.2w
  FormatSpecOverTolerance = %+.2w
  FormatSpecUnderTolerance = %+.2w
  Inverted = false
  LineAngle = 0
  LockPosition = false
  MeasureType = 1
  OverTolerance = 0
  References2D = -> [View012]
  Rotation = 0
  ScaleType = 0
  TheoreticalExact = false
  Type = 2
  UnderTolerance = 0
  X = 34.4166
  Y = -1.24078
FEATURE [TechDraw::DrawViewDimension] Dimension024
  AngleOverride = false
  Arbitrary = false
  ArbitraryTolerances = false
  EqualTolerance = true
  ExtensionAngle = 0
  FormatSpec = %.2w
  FormatSpecOverTolerance = %+.2w
  FormatSpecUnderTolerance = %+.2w
  Inverted = false
  LineAngle = 0
  LockPosition = false
  MeasureType = 1
  OverTolerance = 0
  References2D = -> [View010]
  Rotation = 0
  ScaleType = 0
  TheoreticalExact = false
  Type = 2
  UnderTolerance = 0
  X = 31.9745
  Y = -0.091374
FEATURE [TechDraw::DrawViewDimension] Dimension025
  AngleOverride = false
  Arbitrary = false
  ArbitraryTolerances = false
  EqualTolerance = true
  ExtensionAngle = 0
  FormatSpec = %.2w
  FormatSpecOverTolerance = %+.2w
  FormatSpecUnderTolerance = %+.2w
  Inverted = false
  LineAngle = 0
  LockPosition = false
  MeasureType = 1
  OverTolerance = 0
  References2D = -> [View011]
  Rotation = 0
  ScaleType = 0
  TheoreticalExact = false
  Type = 1
  UnderTolerance = 0
  X = 1.52551
  Y = -56.1623
FEATURE [TechDraw::DrawViewDimension] Dimension026
  AngleOverride = false
  Arbitrary = false
  ArbitraryTolerances = false
  EqualTolerance = true
  ExtensionAngle = 0
  FormatSpec = %.2w
  FormatSpecOverTolerance = %+.2w
  FormatSpecUnderTolerance = %+.2w
  Inverted = false
  LineAngle = 0
  LockPosition = false
  MeasureType = 1
  OverTolerance = 0
  References2D = -> [View011]
  Rotation = 0
  ScaleType = 0
  TheoreticalExact = false
  Type = 2
  UnderTolerance = 0
  X = 50.0819
  Y = 3.38356
FEATURE [TechDraw::DrawViewDimension] Dimension027
  AngleOverride = false
  Arbitrary = false
  ArbitraryTolerances = false
  EqualTolerance = true
  ExtensionAngle = 0
  FormatSpec = %.2w
  FormatSpecOverTolerance = %+.2w
  FormatSpecUnderTolerance = %+.2w
  Inverted = false
  LineAngle = 0
  LockPosition = false
  MeasureType = 1
  OverTolerance = 0
  References2D = -> [View002]
  Rotation = 0
  ScaleType = 0
  TheoreticalExact = false
  Type = 1
  UnderTolerance = 0
  X = -41.6984
  Y = 34.4584
FEATURE [Part::Mirroring] Part__Mirroring  label="Link002 (Mirror #1)"
  Base = (0,0,0)
  Normal = (1,0,0)
  Source = -> Link002
FEATURE [TechDraw::DrawViewPart] View007
  CoarseView = false
  Direction = (0,0,1)
  Focus = 100
  HardHidden = false
  IsoCount = 0
  IsoHidden = false
  IsoVisible = false
  LockPosition = false
  Perspective = false
  Rotation = 0
  ScaleType = 0
  SeamHidden = false
  SeamVisible = true
  SmoothHidden = false
  SmoothVisible = true
  X = 182.567
  XDirection = (1,0,0)
  XSource = -> [Link002]
  Y = 105.348
FEATURE [TechDraw::DrawViewPart] View008
  CoarseView = false
  Direction = (0,-1,0)
  Focus = 100
  HardHidden = false
  IsoCount = 0
  IsoHidden = false
  IsoVisible = false
  LockPosition = false
  Perspective = false
  Rotation = 0
  ScaleType = 0
  SeamHidden = false
  SeamVisible = true
  SmoothHidden = false
  SmoothVisible = true
  X = 55.3363
  XDirection = (1,0,0)
  XSource = -> [Link002]
  Y = 101.176
FEATURE [TechDraw::DrawViewDimension] Dimension021
  AngleOverride = false
  Arbitrary = false
  ArbitraryTolerances = false
  EqualTolerance = true
  ExtensionAngle = 0
  FormatSpec = %.2w
  FormatSpecOverTolerance = %+.2w
  FormatSpecUnderTolerance = %+.2w
  Inverted = false
  LineAngle = 0
  LockPosition = false
  MeasureType = 1
  OverTolerance = 0
  References2D = -> [View008]
  Rotation = 0
  ScaleType = 0
  TheoreticalExact = false
  Type = 2
  UnderTolerance = 0
  X = 62.7697
  Y = 0.613537
FEATURE [TechDraw::DrawViewDimension] Dimension022
  AngleOverride = false
  Arbitrary = false
  ArbitraryTolerances = false
  EqualTolerance = true
  ExtensionAngle = 0
  FormatSpec = %.2w
  FormatSpecOverTolerance = %+.2w
  FormatSpecUnderTolerance = %+.2w
  Inverted = false
  LineAngle = 0
  LockPosition = false
  MeasureType = 1
  OverTolerance = 0
  References2D = -> [View008]
  Rotation = 0
  ScaleType = 0
  TheoreticalExact = false
  Type = 1
  UnderTolerance = 0
  X = -1.18229
  Y = -78.1163
FEATURE [TechDraw::DrawViewPart] View016
  CoarseView = false
  Direction = (0,0,1)
  Focus = 100
  HardHidden = false
  IsoCount = 0
  IsoHidden = false
  IsoVisible = false
  LockPosition = false
  Perspective = false
  Rotation = 0
  ScaleType = 0
  SeamHidden = false
  SeamVisible = true
  SmoothHidden = false
  SmoothVisible = true
  Source = -> [Part__Mirroring]
  X = 211.281
  XDirection = (1,0,0)
  Y = 108.839
FEATURE [TechDraw::DrawViewPart] View017
  CoarseView = false
  Direction = (0,-1,-1.68587e-07)
  Focus = 100
  HardHidden = false
  IsoCount = 0
  IsoHidden = false
  IsoVisible = false
  LockPosition = false
  Perspective = false
  Rotation = 0
  ScaleType = 0
  SeamHidden = false
  SeamVisible = true
  SmoothHidden = false
  SmoothVisible = true
  Source = -> [Part__Mirroring]
  X = 95.309
  XDirection = (1,0,0)
  Y = 105.257
FEATURE [TechDraw::DrawViewDimension] Dimension033
  AngleOverride = false
  Arbitrary = false
  ArbitraryTolerances = false
  EqualTolerance = true
  ExtensionAngle = 0
  FormatSpec = %.2w
  FormatSpecOverTolerance = %+.2w
  FormatSpecUnderTolerance = %+.2w
  Inverted = false
  LineAngle = 0
  LockPosition = false
  MeasureType = 1
  OverTolerance = 0
  References2D = -> [View017]
  Rotation = 0
  ScaleType = 0
  TheoreticalExact = false
  Type = 1
  UnderTolerance = 0
  X = 1.85912
  Y = -60.5562
FEATURE [Part::Mirroring] Part__Mirroring001  label="Link003 (Mirror #2)"
  Base = (0,0,0)
  Normal = (1,0,0)
  Source = -> Link003
FEATURE [TechDraw::DrawViewPart] View018
  CoarseView = false
  Direction = (0,0,1)
  Focus = 100
  HardHidden = false
  IsoCount = 0
  IsoHidden = false
  IsoVisible = false
  LockPosition = false
  Perspective = false
  Rotation = 0
  ScaleType = 0
  SeamHidden = false
  SeamVisible = true
  SmoothHidden = false
  SmoothVisible = true
  Source = -> [Part__Mirroring001]
  X = 148.5
  XDirection = (1,0,0)
  Y = 105
FEATURE [TechDraw::DrawViewPart] View019
  CoarseView = false
  Direction = (0,-1,-1.68587e-07)
  Focus = 100
  HardHidden = false
  IsoCount = 0
  IsoHidden = false
  IsoVisible = false
  LockPosition = false
  Perspective = false
  Rotation = 90
  Scale = 0.23
  ScaleType = 2
  SeamHidden = false
  SeamVisible = true
  SmoothHidden = false
  SmoothVisible = true
  Source = -> [Part__Mirroring001]
  X = 152.64
  XDirection = (1,0,0)
  Y = 74.3656
FEATURE [TechDraw::DrawViewPart] View020
  CoarseView = false
  Direction = (1,1.78814e-07,-5.9605e-08)
  Focus = 100
  HardHidden = false
  IsoCount = 0
  IsoHidden = false
  IsoVisible = false
  LockPosition = false
  Perspective = false
  Rotation = 90
  Scale = 0.23
  ScaleType = 2
  SeamHidden = false
  SeamVisible = true
  SmoothHidden = false
  SmoothVisible = true
  Source = -> [Part__Mirroring001]
  X = 153.6
  XDirection = (-1.78814e-07,1,1.19209e-07)
  Y = 156.646
FEATURE [TechDraw::DrawViewDimension] Dimension036
  AngleOverride = false
  Arbitrary = false
  ArbitraryTolerances = false
  EqualTolerance = true
  ExtensionAngle = 0
  FormatSpec = %.2w
  FormatSpecOverTolerance = %+.2w
  FormatSpecUnderTolerance = %+.2w
  Inverted = false
  LineAngle = 0
  LockPosition = false
  MeasureType = 1
  OverTolerance = 0
  References2D = -> [View020]
  Rotation = 0
  ScaleType = 0
  TheoreticalExact = false
  Type = 2
  UnderTolerance = 0
  X = -136.929
  Y = 2.70598
FEATURE [TechDraw::DrawViewDimension] Dimension037
  AngleOverride = false
  Arbitrary = false
  ArbitraryTolerances = false
  EqualTolerance = true
  ExtensionAngle = 0
  FormatSpec = %.2w
  FormatSpecOverTolerance = %+.2w
  FormatSpecUnderTolerance = %+.2w
  Inverted = false
  LineAngle = 0
  LockPosition = false
  MeasureType = 1
  OverTolerance = 0
  References2D = -> [View019]
  Rotation = 0
  ScaleType = 0
  TheoreticalExact = false
  Type = 2
  UnderTolerance = 0
  X = -136.923
  Y = 1.72338
FEATURE [TechDraw::DrawViewDimension] Dimension038
  AngleOverride = false
  Arbitrary = false
  ArbitraryTolerances = false
  EqualTolerance = true
  ExtensionAngle = 0
  FormatSpec = %.2w
  FormatSpecOverTolerance = %+.2w
  FormatSpecUnderTolerance = %+.2w
  Inverted = false
  LineAngle = 0
  LockPosition = false
  MeasureType = 1
  OverTolerance = 0
  References2D = -> [View018]
  Rotation = 0
  ScaleType = 0
  TheoreticalExact = false
  Type = 2
  UnderTolerance = 0
  X = -33.4228
  Y = 3.81821
FEATURE [TechDraw::DrawViewDimension] Dimension039
  AngleOverride = false
  Arbitrary = false
  ArbitraryTolerances = false
  EqualTolerance = true
  ExtensionAngle = 0
  FormatSpec = %.2w
  FormatSpecOverTolerance = %+.2w
  FormatSpecUnderTolerance = %+.2w
  Inverted = false
  LineAngle = 0
  LockPosition = false
  MeasureType = 1
  OverTolerance = 0
  References2D = -> [View018]
  Rotation = 0
  ScaleType = 0
  TheoreticalExact = false
  Type = 1
  UnderTolerance = 0
  X = -0.202802
  Y = 19.9705
FEATURE [App::Link] Link005  label="pillar2_link"
  LinkedObject = -> <external composit_full_size2part.FCStd>#Body065
  expr: LinkedObject = <<composit_full_size2part>>#<<pillar2_material_0.40ansi>>._self
FEATURE [App::Link] Link006  label="pillar_top_element_link"
  LinkedObject = -> <external composit_full_size2part.FCStd>#Body064
  expr: LinkedObject = <<composit_full_size2part>>#<<pillar_top_element_material_0.40ansi>>._self
FEATURE [App::Link] Link007  label="top_dec_corner_link"
  LinkedObject = -> <external composit_full_size2part.FCStd>#Body066
  expr: LinkedObject = composit_full_size2part#<<top_dec_corner_material_0.40ansi>>._self
FEATURE [Part::Feature] Unfold  label="pillar_bottom_Unfold"
  shape: bbox 101 x 131.4 x 2.002 mm, 19 faces (baked)
FEATURE [Sketcher::SketchObject] Unfold_Sketch  label="pillar_bottom_Sketch"
  FullyConstrained = false
  sketch-geometry (17):
    g0: ArcOfCircle CenterX=38 CenterY=103.898 CenterZ=0 NormalX=0 NormalY=0 NormalZ=1 AngleXU=-5e-16 Radius=2.5 StartAngle=1.5708 EndAngle=3.14159
    g1: ArcOfCircle CenterX=-21.7033 CenterY=103.898 CenterZ=0 NormalX=0 NormalY=0 NormalZ=1 AngleXU=-5e-16 Radius=57.2033 StartAngle=5.41052 EndAngle=6.28319
    g2: LineSegment StartX=38 StartY=106.398 StartZ=0 EndX=48 EndY=106.398 EndZ=0
    g3: LineSegment StartX=-46.9279 StartY=8.05867 StartZ=0 EndX=15.0663 EndY=60.0779 EndZ=0
    g4: ArcOfCircle CenterX=48 CenterY=103.898 CenterZ=0 NormalX=0 NormalY=0 NormalZ=1 AngleXU=-5e-16 Radius=2.5 StartAngle=0 EndAngle=1.5708
    g5: ArcOfCircle CenterX=-40.5 CenterY=0.39823 CenterZ=0 NormalX=0 NormalY=0 NormalZ=1 AngleXU=-5e-16 Radius=10 StartAngle=2.26893 EndAngle=3.14159
    g6: LineSegment StartX=-50.5 StartY=-4 StartZ=0 EndX=-50.5 EndY=0.39823 EndZ=0
    g7: ArcOfCircle CenterX=-29.5 CenterY=-4 CenterZ=0 NormalX=0 NormalY=0 NormalZ=1 AngleXU=0 Radius=21 StartAngle=3.14159 EndAngle=4.71239
    g8: LineSegment StartX=29.5 StartY=-25 StartZ=0 EndX=-29.5 EndY=-25 EndZ=0
    g9: ArcOfCircle CenterX=29.5 CenterY=-4 CenterZ=0 NormalX=0 NormalY=0 NormalZ=1 AngleXU=0 Radius=21 StartAngle=4.71239 EndAngle=6.28319
    g10: Circle CenterX=40 CenterY=-12 CenterZ=0 NormalX=0 NormalY=0 NormalZ=1 AngleXU=-3.14159 Radius=2.75
    g11: Circle CenterX=-40 CenterY=-12 CenterZ=0 NormalX=0 NormalY=0 NormalZ=1 AngleXU=-3.14159 Radius=2.75
    g12: Circle CenterX=43 CenterY=96.3982 CenterZ=0 NormalX=0 NormalY=0 NormalZ=1 AngleXU=-5e-16 Radius=1.7
    g13: Circle CenterX=43 CenterY=67.7316 CenterZ=0 NormalX=0 NormalY=0 NormalZ=1 AngleXU=-5e-16 Radius=1.7
    g14: Circle CenterX=43 CenterY=39.0649 CenterZ=0 NormalX=0 NormalY=0 NormalZ=1 AngleXU=-5e-16 Radius=1.7
    g15: Circle CenterX=43 CenterY=10.3982 CenterZ=0 NormalX=0 NormalY=0 NormalZ=1 AngleXU=-5e-16 Radius=1.7
    g16: LineSegment StartX=50.5 StartY=103.898 StartZ=0 EndX=50.5 EndY=-4 EndZ=0
FEATURE [Sketcher::SketchObject] Unfold_Sketch_bends  label="pillar_bottom_bends"
  FullyConstrained = false
  Placement = pos=(0,-0.442186,0.775112) rot=(1,0,0;0.518431rad)
  sketch-geometry (1):
    g0: LineSegment StartX=50.5 StartY=-1.56424 StartZ=0 EndX=-50.5 EndY=-1.56424 EndZ=0
FEATURE [Part::Feature] Unfold005  label="pillar_top_element_Unfold"
  shape: bbox 114.8 x 150.4 x 2.247 mm, 34 faces (baked)
FEATURE [Sketcher::SketchObject] Unfold_Sketch005  label="pillar_top_element_Sketch"
  FullyConstrained = false
  sketch-geometry (32):
    g0: LineSegment StartX=1.39823 StartY=57.3982 StartZ=0 EndX=75.3982 EndY=57.3982 EndZ=0
    g1: BSplineCurve PolesCount=34 KnotsCount=9 Degree=5 IsPeriodic=0
    g2: BSplineCurve PolesCount=34 KnotsCount=9 Degree=5 IsPeriodic=0
    g3: LineSegment StartX=-3.60177 StartY=52.3982 StartZ=0 EndX=-3.60177 EndY=36.3982 EndZ=0
    g4: LineSegment StartX=-3.60177 StartY=36.3982 StartZ=0 EndX=0.39823 EndY=36.3982 EndZ=0
    g5: LineSegment StartX=0.39823 StartY=36.3982 StartZ=0 EndX=0.39823 EndY=32 EndZ=0
    g6: LineSegment StartX=1.39823 StartY=-57.3982 StartZ=0 EndX=75.3982 EndY=-57.3982 EndZ=0
    g7: BSplineCurve PolesCount=34 KnotsCount=9 Degree=5 IsPeriodic=0
    g8: BSplineCurve PolesCount=34 KnotsCount=9 Degree=5 IsPeriodic=0
    g9: LineSegment StartX=-3.60177 StartY=-36.3982 StartZ=0 EndX=-3.60177 EndY=-52.3982 EndZ=0
    g10: BSplineCurve PolesCount=2 KnotsCount=2 Degree=1 IsPeriodic=0
    g11: LineSegment StartX=0.39823 StartY=-32 StartZ=0 EndX=0.39823 EndY=-36.3982 EndZ=0
    g12: ArcOfCircle CenterX=-65 CenterY=-27 CenterZ=0 NormalX=0 NormalY=0 NormalZ=1 AngleXU=1.5708 Radius=5 StartAngle=1.5708 EndAngle=3.14159
    g13: LineSegment StartX=-70 StartY=-27 StartZ=0 EndX=-70 EndY=27 EndZ=0
    g14: ArcOfCircle CenterX=-65 CenterY=27 CenterZ=0 NormalX=0 NormalY=0 NormalZ=1 AngleXU=1.5708 Radius=5 StartAngle=0 EndAngle=1.5708
    g15: LineSegment StartX=1.39823 StartY=8.5 StartZ=0 EndX=1.39823 EndY=-8.5 EndZ=0
    g16: LineSegment StartX=-18 StartY=-8.5 StartZ=0 EndX=-18 EndY=8.5 EndZ=0
    g17: Circle CenterX=6.39823 CenterY=42.3982 CenterZ=0 NormalX=0 NormalY=0 NormalZ=1 AngleXU=-1.5708 Radius=1.7
    g18: Circle CenterX=6.39823 CenterY=-42.3982 CenterZ=0 NormalX=0 NormalY=0 NormalZ=-1 AngleXU=1.5708 Radius=1.7
    g19: Circle CenterX=76.3982 CenterY=42.3982 CenterZ=0 NormalX=0 NormalY=0 NormalZ=1 AngleXU=-1.5708 Radius=1.7
    g20: Circle CenterX=76.3982 CenterY=-42.3982 CenterZ=0 NormalX=0 NormalY=0 NormalZ=-1 AngleXU=1.5708 Radius=1.7
    g21: Circle CenterX=6.39823 CenterY=0 CenterZ=0 NormalX=0 NormalY=0 NormalZ=-1 AngleXU=-1.5708 Radius=1.7
    g22: Circle CenterX=76.3982 CenterY=0 CenterZ=0 NormalX=0 NormalY=0 NormalZ=-1 AngleXU=-1.5708 Radius=1.7
    g23: Circle CenterX=-60 CenterY=25 CenterZ=0 NormalX=0 NormalY=0 NormalZ=1 AngleXU=1.5708 Radius=1.7
    g24: Circle CenterX=-60 CenterY=-25 CenterZ=0 NormalX=0 NormalY=0 NormalZ=1 AngleXU=1.5708 Radius=1.7
    g25: Circle CenterX=-25 CenterY=0 CenterZ=0 NormalX=0 NormalY=0 NormalZ=1 AngleXU=1.5708 Radius=1.7
    g26: Circle CenterX=7.39823 CenterY=-12.5 CenterZ=0 NormalX=0 NormalY=0 NormalZ=1 AngleXU=-1.5708 Radius=1.7
    g27: LineSegment StartX=-65 StartY=32 StartZ=0 EndX=0.39823 EndY=32 EndZ=0
    g28: LineSegment StartX=0.39823 StartY=-32 StartZ=0 EndX=-65 EndY=-32 EndZ=0
    g29: LineSegment StartX=80.3982 StartY=52.3982 StartZ=0 EndX=80.3982 EndY=-52.3982 EndZ=0
    g30: LineSegment StartX=1.39823 StartY=-8.5 StartZ=0 EndX=-18 EndY=-8.5 EndZ=0
    g31: LineSegment StartX=-18 StartY=8.5 StartZ=0 EndX=1.39823 EndY=8.5 EndZ=0
FEATURE [Sketcher::SketchObject] Unfold_Sketch_bends005  label="pillar_top_element_bends"
  FullyConstrained = false
  sketch-geometry (4):
    g0: LineSegment StartX=-1.80089 StartY=8.5 StartZ=0 EndX=-1.80089 EndY=32 EndZ=0
    g1: LineSegment StartX=80.3982 StartY=34.1991 StartZ=0 EndX=0.39823 EndY=34.1991 EndZ=0
    g2: LineSegment StartX=80.3982 StartY=-34.1991 StartZ=0 EndX=0.39823 EndY=-34.1991 EndZ=0
    g3: LineSegment StartX=-1.80089 StartY=-32 StartZ=0 EndX=-1.80089 EndY=-8.5 EndZ=0
FEATURE [Part::Feature] Unfold006  label="pillar2_Unfold"
  Placement = pos=(0,0,0) rot=(0.57735,-0.57735,0.57735;4.18879rad)
  shape: bbox 1684 x 67.4 x 2.247 mm, 46 faces (baked)
FEATURE [Sketcher::SketchObject] Unfold_Sketch006  label="pillar2_Sketch"
  FullyConstrained = false
  sketch-geometry (44):
    g0: LineSegment StartX=5 StartY=33.6982 StartZ=0 EndX=1589 EndY=33.6982 EndZ=0
    g1: BSplineCurve PolesCount=34 KnotsCount=9 Degree=5 IsPeriodic=0
    g2: BSplineCurve PolesCount=34 KnotsCount=9 Degree=5 IsPeriodic=0
    g3: LineSegment StartX=0 StartY=-28.6982 StartZ=0 EndX=0 EndY=28.6982 EndZ=0
    g4: BSplineCurve PolesCount=34 KnotsCount=9 Degree=5 IsPeriodic=0
    g5: LineSegment StartX=5 StartY=-33.6982 StartZ=0 EndX=1589 EndY=-33.6982 EndZ=0
    g6: BSplineCurve PolesCount=34 KnotsCount=9 Degree=5 IsPeriodic=0
    g7: LineSegment StartX=1594 StartY=-28.6982 StartZ=0 EndX=1594 EndY=-14.3 EndZ=0
    g8: LineSegment StartX=1596 StartY=-14.3 StartZ=0 EndX=1594 EndY=-14.3 EndZ=0
    g9: LineSegment StartX=1596 StartY=-29 StartZ=0 EndX=1596 EndY=-14.3 EndZ=0
    g10: ArcOfCircle CenterX=1599 CenterY=-29 CenterZ=0 NormalX=0 NormalY=0 NormalZ=1 AngleXU=1.5708 Radius=3 StartAngle=1.5708 EndAngle=3.14159
    g11: LineSegment StartX=1681 StartY=-32 StartZ=0 EndX=1599 EndY=-32 EndZ=0
    g12: ArcOfCircle CenterX=1681 CenterY=-29 CenterZ=0 NormalX=0 NormalY=0 NormalZ=1 AngleXU=1.5708 Radius=3 StartAngle=3.14159 EndAngle=4.71239
    g13: LineSegment StartX=1684 StartY=29 StartZ=0 EndX=1684 EndY=-29 EndZ=0
    g14: ArcOfCircle CenterX=1681 CenterY=29 CenterZ=0 NormalX=0 NormalY=0 NormalZ=1 AngleXU=1.5708 Radius=3 StartAngle=4.71239 EndAngle=6.28319
    g15: LineSegment StartX=1599 StartY=32 StartZ=0 EndX=1681 EndY=32 EndZ=0
    g16: ArcOfCircle CenterX=1599 CenterY=29 CenterZ=0 NormalX=0 NormalY=0 NormalZ=1 AngleXU=1.5708 Radius=3 StartAngle=0 EndAngle=1.5708
    g17: LineSegment StartX=1596 StartY=14.3 StartZ=0 EndX=1596 EndY=29 EndZ=0
    g18: LineSegment StartX=1594 StartY=14.3 StartZ=0 EndX=1596 EndY=14.3 EndZ=0
    g19: LineSegment StartX=1594 StartY=14.3 StartZ=0 EndX=1594 EndY=28.6982 EndZ=0
    g20: Circle CenterX=470 CenterY=0 CenterZ=0 NormalX=0 NormalY=0 NormalZ=-1 AngleXU=1.5708 Radius=1.8
    g21: Circle CenterX=1605 CenterY=12.5 CenterZ=0 NormalX=0 NormalY=0 NormalZ=-1 AngleXU=1.5708 Radius=1.8
    g22: Circle CenterX=1434 CenterY=26.6982 CenterZ=0 NormalX=0 NormalY=0 NormalZ=1 AngleXU=-1.5708 Radius=1.7
    g23: Circle CenterX=1434 CenterY=-26.6982 CenterZ=0 NormalX=0 NormalY=0 NormalZ=-1 AngleXU=1.5708 Radius=1.7
    g24: Circle CenterX=1014 CenterY=26.6982 CenterZ=0 NormalX=0 NormalY=0 NormalZ=1 AngleXU=-1.5708 Radius=1.7
    g25: Circle CenterX=594 CenterY=26.6982 CenterZ=0 NormalX=0 NormalY=0 NormalZ=1 AngleXU=-1.5708 Radius=1.7
    g26: Circle CenterX=1014 CenterY=-26.6982 CenterZ=0 NormalX=0 NormalY=0 NormalZ=-1 AngleXU=1.5708 Radius=1.7
    g27: Circle CenterX=594 CenterY=-26.6982 CenterZ=0 NormalX=0 NormalY=0 NormalZ=-1 AngleXU=1.5708 Radius=1.7
    g28: Circle CenterX=1486 CenterY=0 CenterZ=0 NormalX=0 NormalY=0 NormalZ=1 AngleXU=1.5708 Radius=1.7
    g29: Circle CenterX=1286 CenterY=0 CenterZ=0 NormalX=0 NormalY=0 NormalZ=1 AngleXU=1.5708 Radius=1.7
    g30: Circle CenterX=1086 CenterY=0 CenterZ=0 NormalX=0 NormalY=0 NormalZ=1 AngleXU=1.5708 Radius=1.7
    g31: Circle CenterX=886 CenterY=0 CenterZ=0 NormalX=0 NormalY=0 NormalZ=1 AngleXU=1.5708 Radius=1.7
    g32: Circle CenterX=686 CenterY=0 CenterZ=0 NormalX=0 NormalY=0 NormalZ=1 AngleXU=1.5708 Radius=1.7
    g33: Circle CenterX=1674 CenterY=0 CenterZ=0 NormalX=0 NormalY=0 NormalZ=1 AngleXU=1.5708 Radius=1.7
    g34: Circle CenterX=1604 CenterY=0 CenterZ=0 NormalX=0 NormalY=0 NormalZ=1 AngleXU=1.5708 Radius=1.7
    g35: Circle CenterX=100 CenterY=26.1982 CenterZ=0 NormalX=0 NormalY=0 NormalZ=1 AngleXU=-3.14159 Radius=1.7
    g36: Circle CenterX=42.6667 CenterY=-26.1982 CenterZ=0 NormalX=0 NormalY=0 NormalZ=1 AngleXU=-3.14159 Radius=1.7
    g37: Circle CenterX=71.3333 CenterY=-26.1982 CenterZ=0 NormalX=0 NormalY=0 NormalZ=1 AngleXU=-3.14159 Radius=1.7
    g38: Circle CenterX=100 CenterY=-26.1982 CenterZ=0 NormalX=0 NormalY=0 NormalZ=1 AngleXU=-3.14159 Radius=1.7
    g39: Circle CenterX=42.6667 CenterY=26.1982 CenterZ=0 NormalX=0 NormalY=0 NormalZ=1 AngleXU=-3.14159 Radius=1.7
    g40: Circle CenterX=71.3333 CenterY=26.1982 CenterZ=0 NormalX=0 NormalY=0 NormalZ=1 AngleXU=-3.14159 Radius=1.7
    g41: Circle CenterX=14 CenterY=-26.1982 CenterZ=0 NormalX=0 NormalY=0 NormalZ=1 AngleXU=-3.14159 Radius=1.7
    g42: Circle CenterX=14 CenterY=26.1982 CenterZ=0 NormalX=0 NormalY=0 NormalZ=1 AngleXU=-3.14159 Radius=1.7
    g43: Circle CenterX=486 CenterY=0 CenterZ=0 NormalX=0 NormalY=0 NormalZ=1 AngleXU=1.5708 Radius=1.7
FEATURE [Sketcher::SketchObject] Unfold_Sketch_bends006  label="pillar2_bends"
  FullyConstrained = false
  sketch-geometry (2):
    g0: LineSegment StartX=1594 StartY=-16.4991 StartZ=0 EndX=0 EndY=-16.4991 EndZ=0
    g1: LineSegment StartX=1594 StartY=16.4991 StartZ=0 EndX=0 EndY=16.4991 EndZ=0
FEATURE [PartDesign::FeatureBase] BaseFeature
  BaseFeature = -> Unfold006
  Placement = pos=(0,0,0) rot=(0.57735,-0.57735,0.57735;4.18879rad)
  expr: Placement = Unfold006.Placement
FEATURE [PartDesign::Body] Body  label="pillar2_body"
  BaseFeature = -> Unfold006
  Group = -> [BaseFeature]
  Origin = -> Origin
  Tip = -> BaseFeature
FEATURE [Part::Mirroring] Part__Mirroring003  label="pillar_bottom_Unfold (Mirror #4)"
  Base = (0,0,0)
  Normal = (1,0,0)
  Source = -> Unfold
FEATURE [Sketcher::SketchObject] MirroredSketch
  FullyConstrained = false
  Placement = pos=(0,-0.442186,0.775112) rot=(1,0,0;0.518432rad)
  sketch-geometry (1):
    g0: LineSegment StartX=-50.5 StartY=-1.56424 StartZ=0 EndX=50.5 EndY=-1.56424 EndZ=0
FEATURE [Sketcher::SketchObject] MirroredSketch002
  FullyConstrained = false
  sketch-geometry (17):
    g0: ArcOfCircle CenterX=-38 CenterY=103.898 CenterZ=0 NormalX=0 NormalY=0 NormalZ=1 AngleXU=-5e-16 Radius=2.5 StartAngle=5e-16 EndAngle=1.5708
    g1: ArcOfCircle CenterX=21.7033 CenterY=103.898 CenterZ=0 NormalX=0 NormalY=0 NormalZ=1 AngleXU=-5e-16 Radius=57.2033 StartAngle=3.14159 EndAngle=4.01426
    g2: LineSegment StartX=-38 StartY=106.398 StartZ=0 EndX=-48 EndY=106.398 EndZ=0
    g3: LineSegment StartX=46.9279 StartY=8.05867 StartZ=0 EndX=-15.0663 EndY=60.0779 EndZ=0
    g4: ArcOfCircle CenterX=-48 CenterY=103.898 CenterZ=0 NormalX=0 NormalY=0 NormalZ=1 AngleXU=-5e-16 Radius=2.5 StartAngle=1.5708 EndAngle=3.14159
    g5: ArcOfCircle CenterX=40.5 CenterY=0.39823 CenterZ=0 NormalX=0 NormalY=0 NormalZ=1 AngleXU=-5e-16 Radius=10 StartAngle=1.1e-15 EndAngle=0.872665
    g6: LineSegment StartX=50.5 StartY=-4 StartZ=0 EndX=50.5 EndY=0.39823 EndZ=0
    g7: ArcOfCircle CenterX=29.5 CenterY=-4 CenterZ=0 NormalX=0 NormalY=0 NormalZ=1 AngleXU=0 Radius=21 StartAngle=4.71239 EndAngle=6.28319
    g8: LineSegment StartX=-29.5 StartY=-25 StartZ=0 EndX=29.5 EndY=-25 EndZ=0
    g9: ArcOfCircle CenterX=-29.5 CenterY=-4 CenterZ=0 NormalX=0 NormalY=0 NormalZ=1 AngleXU=0 Radius=21 StartAngle=3.14159 EndAngle=4.71239
    g10: Circle CenterX=-40 CenterY=-12 CenterZ=0 NormalX=0 NormalY=0 NormalZ=1 AngleXU=-3.14159 Radius=2.75
    g11: Circle CenterX=40 CenterY=-12 CenterZ=0 NormalX=0 NormalY=0 NormalZ=1 AngleXU=-3.14159 Radius=2.75
    g12: Circle CenterX=-43 CenterY=96.3982 CenterZ=0 NormalX=0 NormalY=0 NormalZ=1 AngleXU=-5e-16 Radius=1.7
    g13: Circle CenterX=-43 CenterY=67.7316 CenterZ=0 NormalX=0 NormalY=0 NormalZ=1 AngleXU=-5e-16 Radius=1.7
    g14: Circle CenterX=-43 CenterY=39.0649 CenterZ=0 NormalX=0 NormalY=0 NormalZ=1 AngleXU=-5e-16 Radius=1.7
    g15: Circle CenterX=-43 CenterY=10.3982 CenterZ=0 NormalX=0 NormalY=0 NormalZ=1 AngleXU=-5e-16 Radius=1.7
    g16: LineSegment StartX=-50.5 StartY=103.898 StartZ=0 EndX=-50.5 EndY=-4 EndZ=0
FEATURE [TechDraw::DrawViewPart] View009
  CoarseView = false
  Direction = (1,-3.8743e-07,2.68221e-07)
  Focus = 100
  HardHidden = false
  IsoCount = 0
  IsoHidden = false
  IsoVisible = false
  LockPosition = false
  Perspective = false
  Rotation = 0
  ScaleType = 0
  SeamHidden = false
  SeamVisible = true
  SmoothHidden = false
  SmoothVisible = true
  X = 267.388
  XDirection = (3.8743e-07,1,-3.57628e-07)
  XSource = -> [Link002]
  Y = 102.914
FEATURE [TechDraw::DrawViewDimension] Dimension040
  AngleOverride = false
  Arbitrary = false
  ArbitraryTolerances = false
  EqualTolerance = true
  ExtensionAngle = 0
  FormatSpec = %.2w
  FormatSpecOverTolerance = %+.2w
  FormatSpecUnderTolerance = %+.2w
  Inverted = false
  LineAngle = 0
  LockPosition = false
  MeasureType = 1
  OverTolerance = 0
  References2D = -> [View009]
  Rotation = 0
  ScaleType = 0
  TheoreticalExact = false
  Type = 1
  UnderTolerance = 0
  X = -0.582067
  Y = -56.83
FEATURE [TechDraw::DrawViewDimension] Dimension041
  AngleOverride = false
  Arbitrary = false
  ArbitraryTolerances = false
  EqualTolerance = true
  ExtensionAngle = 0
  FormatSpec = %.2w
  FormatSpecOverTolerance = %+.2w
  FormatSpecUnderTolerance = %+.2w
  Inverted = false
  LineAngle = 0
  LockPosition = false
  MeasureType = 1
  OverTolerance = 0
  References2D = -> [View009]
  Rotation = 0
  ScaleType = 0
  TheoreticalExact = false
  Type = 2
  UnderTolerance = 0
  X = 19.413
  Y = 1.18928
FEATURE [TechDraw::DrawViewDimension] Dimension042
  AngleOverride = false
  Arbitrary = false
  ArbitraryTolerances = false
  EqualTolerance = true
  ExtensionAngle = 0
  FormatSpec = %.2w
  FormatSpecOverTolerance = %+.2w
  FormatSpecUnderTolerance = %+.2w
  Inverted = false
  LineAngle = 0
  LockPosition = false
  MeasureType = 1
  OverTolerance = 0
  References2D = -> [View017]
  Rotation = 0
  ScaleType = 0
  TheoreticalExact = false
  Type = 2
  UnderTolerance = 0
  X = -78.7479
  Y = 1.19862
FEATURE [TechDraw::DrawViewDimension] Dimension043
  AngleOverride = false
  Arbitrary = false
  ArbitraryTolerances = false
  EqualTolerance = true
  ExtensionAngle = 0
  FormatSpec = %.2w
  FormatSpecOverTolerance = %+.2w
  FormatSpecUnderTolerance = %+.2w
  Inverted = false
  LineAngle = 0
  LockPosition = false
  MeasureType = 1
  OverTolerance = 0
  References2D = -> [View016]
  Rotation = 0
  ScaleType = 0
  TheoreticalExact = false
  Type = 2
  UnderTolerance = 0
  X = 62.297
  Y = 2.5
FEATURE [TechDraw::DrawViewPart] View024
  CoarseView = false
  Direction = (0,-1,0)
  Focus = 100
  HardHidden = false
  IsoCount = 0
  IsoHidden = false
  IsoVisible = false
  LockPosition = false
  Perspective = false
  Rotation = 90
  Scale = 0.17
  ScaleType = 2
  SeamHidden = false
  SeamVisible = true
  SmoothHidden = false
  SmoothVisible = true
  X = 148.5
  XDirection = (1,0,0)
  XSource = -> [Link005]
  Y = 105
FEATURE [TechDraw::DrawViewPart] View025
  CoarseView = false
  Direction = (0,0,1)
  Focus = 100
  HardHidden = false
  IsoCount = 0
  IsoHidden = false
  IsoVisible = false
  LockPosition = false
  Perspective = false
  Rotation = 0
  ScaleType = 0
  SeamHidden = false
  SeamVisible = true
  SmoothHidden = false
  SmoothVisible = true
  X = 146.937
  XDirection = (0,0,1)
  XSource = -> [Link005]
  Y = 165.018
FEATURE [TechDraw::DrawViewDimension] Dimension055
  AngleOverride = false
  Arbitrary = false
  ArbitraryTolerances = false
  EqualTolerance = true
  ExtensionAngle = 0
  FormatSpec = %.2w
  FormatSpecOverTolerance = %+.2w
  FormatSpecUnderTolerance = %+.2w
  Inverted = false
  LineAngle = 0
  LockPosition = false
  MeasureType = 1
  OverTolerance = 0
  References2D = -> [View025]
  Rotation = 0
  ScaleType = 0
  TheoreticalExact = false
  Type = 1
  UnderTolerance = 0
  X = 0.301071
  Y = 25.1468
FEATURE [TechDraw::DrawViewDimension] Dimension056
  AngleOverride = false
  Arbitrary = false
  ArbitraryTolerances = false
  EqualTolerance = true
  ExtensionAngle = 0
  FormatSpec = %.2w
  FormatSpecOverTolerance = %+.2w
  FormatSpecUnderTolerance = %+.2w
  Inverted = false
  LineAngle = 0
  LockPosition = false
  MeasureType = 1
  OverTolerance = 0
  References2D = -> [View025]
  Rotation = 0
  ScaleType = 0
  TheoreticalExact = false
  Type = 1
  UnderTolerance = 0
  X = -0.832609
  Y = -12.6313
FEATURE [TechDraw::DrawViewDimension] Dimension057
  AngleOverride = false
  Arbitrary = false
  ArbitraryTolerances = false
  EqualTolerance = true
  ExtensionAngle = 0
  FormatSpec = %.2w
  FormatSpecOverTolerance = %+.2w
  FormatSpecUnderTolerance = %+.2w
  Inverted = false
  LineAngle = 0
  LockPosition = false
  MeasureType = 1
  OverTolerance = 0
  References2D = -> [View025]
  Rotation = 0
  ScaleType = 0
  TheoreticalExact = false
  Type = 2
  UnderTolerance = 0
  X = 26.2539
  Y = 3.00178
FEATURE [TechDraw::DrawViewDimension] Dimension058
  AngleOverride = false
  Arbitrary = false
  ArbitraryTolerances = false
  EqualTolerance = true
  ExtensionAngle = 0
  FormatSpec = %.2w
  FormatSpecOverTolerance = %+.2w
  FormatSpecUnderTolerance = %+.2w
  Inverted = false
  LineAngle = 0
  LockPosition = false
  MeasureType = 1
  OverTolerance = 0
  References2D = -> [View024]
  Rotation = 0
  ScaleType = 0
  TheoreticalExact = false
  Type = 2
  UnderTolerance = 0
  X = 137.237
  Y = -9.30548
FEATURE [TechDraw::DrawViewDimension] Dimension059
  AngleOverride = false
  Arbitrary = false
  ArbitraryTolerances = false
  EqualTolerance = true
  ExtensionAngle = 0
  FormatSpec = %.2w
  FormatSpecOverTolerance = %+.2w
  FormatSpecUnderTolerance = %+.2w
  Inverted = false
  LineAngle = 0
  LockPosition = false
  MeasureType = 1
  OverTolerance = 0
  References2D = -> [View024]
  Rotation = 0
  ScaleType = 0
  TheoreticalExact = false
  Type = 1
  UnderTolerance = 0
  X = 1.05581
  Y = -21.2289
FEATURE [TechDraw::DrawViewDimension] Dimension060
  AngleOverride = false
  Arbitrary = false
  ArbitraryTolerances = false
  EqualTolerance = true
  ExtensionAngle = 0
  FormatSpec = R%.2w
  FormatSpecOverTolerance = %+.2w
  FormatSpecUnderTolerance = %+.2w
  Inverted = false
  LineAngle = 0
  LockPosition = false
  MeasureType = 1
  OverTolerance = 0
  References2D = -> [View025]
  Rotation = 0
  ScaleType = 0
  TheoreticalExact = false
  Type = 4
  UnderTolerance = 0
  X = -4.85689
  Y = 5.6895
FEATURE [TechDraw::DrawViewDimension] Dimension061
  AngleOverride = false
  Arbitrary = false
  ArbitraryTolerances = false
  EqualTolerance = true
  ExtensionAngle = 0
  FormatSpec = R%.2w
  FormatSpecOverTolerance = %+.2w
  FormatSpecUnderTolerance = %+.2w
  Inverted = false
  LineAngle = 0
  LockPosition = false
  MeasureType = 1
  OverTolerance = 0
  References2D = -> [View025]
  Rotation = 0
  ScaleType = 0
  TheoreticalExact = false
  Type = 4
  UnderTolerance = 0
  X = 6.93841
  Y = 4.71812
FEATURE [App::Link] Link008  label="top_dec_corner_mirror_link"
  LinkedObject = -> <external composit_full_size2part.FCStd>#Body067
  expr: LinkedObject = composit_full_size2part#<<top_dec_corner_mirror_material_0.40ansi>>._self
FEATURE [Part::Feature] Unfold007  label="top_dec_corner_unfold"
  Placement = pos=(0,0,-1.5) rot=(0.57735,0.57735,0.57735;2.0944rad)
  shape: bbox 96 x 97.46 x 0.5632 mm, 18 faces (baked)
FEATURE [Sketcher::SketchObject] Unfold_Sketch007  label="top_dec_corner_sketch"
  FullyConstrained = false
  sketch-geometry (16):
    g0: LineSegment StartX=-3 StartY=65.4558 StartZ=0 EndX=87 EndY=65.4558 EndZ=0
    g1: BSplineCurve PolesCount=26 KnotsCount=9 Degree=4 IsPeriodic=0
    g2: BSplineCurve PolesCount=26 KnotsCount=9 Degree=4 IsPeriodic=0
    g3: LineSegment StartX=-6 StartY=35.5 StartZ=0 EndX=-6 EndY=62.4558 EndZ=0
    g4: ArcOfCircle CenterX=7.12042 CenterY=35.5 CenterZ=0 NormalX=0 NormalY=0 NormalZ=1 AngleXU=1.5708 Radius=13.1204 StartAngle=1.5708 EndAngle=2.26063
    g5: ArcOfCircle CenterX=-13.1204 CenterY=18.8 CenterZ=0 NormalX=0 NormalY=0 NormalZ=1 AngleXU=1.5708 Radius=13.1204 StartAngle=4.71239 EndAngle=5.40223
    g6: LineSegment StartX=3.921e-13 StartY=-29 StartZ=0 EndX=-2.9421e-12 EndY=18.8 EndZ=0
    g7: ArcOfCircle CenterX=3 CenterY=-29 CenterZ=0 NormalX=0 NormalY=0 NormalZ=1 AngleXU=1.5708 Radius=3 StartAngle=1.5708 EndAngle=3.14159
    g8: LineSegment StartX=3 StartY=-32 StartZ=0 EndX=87 EndY=-32 EndZ=0
    g9: BSplineCurve PolesCount=26 KnotsCount=9 Degree=4 IsPeriodic=0
    g10: LineSegment StartX=90 StartY=-29 StartZ=0 EndX=90 EndY=62.4558 EndZ=0
    g11: Circle CenterX=10 CenterY=50.4558 CenterZ=0 NormalX=0 NormalY=0 NormalZ=1 AngleXU=-1.5708 Radius=1.7
    g12: Circle CenterX=80 CenterY=50.4558 CenterZ=0 NormalX=0 NormalY=0 NormalZ=1 AngleXU=-1.5708 Radius=1.7
    g13: Circle CenterX=80 CenterY=0 CenterZ=0 NormalX=0 NormalY=0 NormalZ=1 AngleXU=-1.5708 Radius=1.7
    g14: Circle CenterX=10 CenterY=0 CenterZ=0 NormalX=0 NormalY=0 NormalZ=1 AngleXU=-1.5708 Radius=1.7
    g15: Circle CenterX=11 CenterY=12.5 CenterZ=0 NormalX=0 NormalY=0 NormalZ=1 AngleXU=-1.5708 Radius=1.7
FEATURE [Sketcher::SketchObject] Unfold_Sketch_bends007  label="top_dec_corner_bends"
  FullyConstrained = false
  Placement = pos=(0,11.8419,17.3383) rot=(-1,0,0;0.599218rad)
  sketch-geometry (1):
    g0: LineSegment StartX=90 StartY=30.7419 StartZ=0 EndX=-6 EndY=30.7419 EndZ=0
FEATURE [Part::Feature] Unfold008  label="top_dec_corner_mirror_unfold"
  Placement = pos=(0,0,-1) rot=(0.57735,0.57735,0.57735;2.0944rad)
  shape: bbox 96 x 96.46 x 1.098 mm, 19 faces (baked)
FEATURE [Sketcher::SketchObject] Unfold_Sketch008  label="top_dec_corner_mirror_sketch"
  FullyConstrained = false
  sketch-geometry (18):
    g0: LineSegment StartX=-3 StartY=-64.4558 StartZ=0 EndX=87 EndY=-64.4558 EndZ=0
    g1: BSplineCurve PolesCount=26 KnotsCount=9 Degree=4 IsPeriodic=0
    g2: BSplineCurve PolesCount=26 KnotsCount=9 Degree=4 IsPeriodic=0
    g3: LineSegment StartX=90 StartY=-61.4558 StartZ=0 EndX=90 EndY=29 EndZ=0
    g4: BSplineCurve PolesCount=26 KnotsCount=9 Degree=4 IsPeriodic=0
    g5: LineSegment StartX=3 StartY=32 StartZ=0 EndX=87 EndY=32 EndZ=0
    g6: ArcOfCircle CenterX=3 CenterY=29 CenterZ=0 NormalX=0 NormalY=0 NormalZ=1 AngleXU=-1.5708 Radius=3 StartAngle=3.14159 EndAngle=4.71239
    g7: LineSegment StartX=3.921e-13 StartY=29 StartZ=0 EndX=-2.9421e-12 EndY=-18.8 EndZ=0
    g8: ArcOfCircle CenterX=-13.1204 CenterY=-18.8 CenterZ=0 NormalX=0 NormalY=0 NormalZ=1 AngleXU=-1.5708 Radius=13.1204 StartAngle=0.880958 EndAngle=1.5708
    g9: ArcOfCircle CenterX=7.12042 CenterY=-35.5 CenterZ=0 NormalX=0 NormalY=0 NormalZ=1 AngleXU=-1.5708 Radius=13.1204 StartAngle=4.02255 EndAngle=4.67427
    g10: BSplineCurve PolesCount=15 KnotsCount=13 Degree=3 IsPeriodic=0
    g11: LineSegment StartX=-6 StartY=-61.4558 StartZ=0 EndX=-6 EndY=-35.443 EndZ=0
    g12: Circle CenterX=80 CenterY=-49.4558 CenterZ=0 NormalX=0 NormalY=0 NormalZ=1 AngleXU=3.14159 Radius=1.7
    g13: Circle CenterX=80 CenterY=0 CenterZ=0 NormalX=0 NormalY=0 NormalZ=1 AngleXU=-1.5708 Radius=1.7
    g14: Circle CenterX=10 CenterY=-49.4558 CenterZ=0 NormalX=0 NormalY=0 NormalZ=1 AngleXU=3.14159 Radius=1.7
    g15: Circle CenterX=10 CenterY=0 CenterZ=0 NormalX=0 NormalY=0 NormalZ=1 AngleXU=-1.5708 Radius=1.7
    g16: Circle CenterX=11 CenterY=12.5 CenterZ=0 NormalX=0 NormalY=0 NormalZ=1 AngleXU=-1.5708 Radius=1.7
    g17: BSplineCurve PolesCount=15 KnotsCount=13 Degree=3 IsPeriodic=0
FEATURE [Sketcher::SketchObject] Unfold_Sketch_bends008  label="top_dec_corner_mirror_bends"
  FullyConstrained = false
  Placement = pos=(0,-14.3075,-17.9103) rot=(-1,0,0;0.674033rad)
  sketch-geometry (1):
    g0: LineSegment StartX=90 StartY=-28.6959 StartZ=0 EndX=-6 EndY=-28.6959 EndZ=0
FEATURE [TechDraw::DrawViewPart] View022
  CoarseView = false
  Direction = (1,0,0)
  Focus = 100
  HardHidden = false
  IsoCount = 0
  IsoHidden = false
  IsoVisible = false
  LockPosition = false
  Perspective = false
  Rotation = 0
  ScaleType = 0
  SeamHidden = false
  SeamVisible = true
  SmoothHidden = false
  SmoothVisible = true
  X = 242.75
  XDirection = (0,1,-1.19209e-07)
  XSource = -> [Link006]
  Y = 105
  expr: X = Template.Width / 4 * 3 + 20 mm
  expr: Y = Template.Height / 2
FEATURE [TechDraw::DrawViewDimension] Dimension053
  AngleOverride = false
  Arbitrary = false
  ArbitraryTolerances = false
  EqualTolerance = true
  ExtensionAngle = 0
  FormatSpec = %.2w
  FormatSpecOverTolerance = %+.2w
  FormatSpecUnderTolerance = %+.2w
  Inverted = false
  LineAngle = 0
  LockPosition = false
  MeasureType = 1
  OverTolerance = 0
  References2D = -> [View022]
  Rotation = 0
  ScaleType = 0
  TheoreticalExact = false
  Type = 1
  UnderTolerance = 0
  X = 0.590062
  Y = -44.5807
FEATURE [TechDraw::DrawViewDimension] Dimension054
  AngleOverride = false
  Arbitrary = false
  ArbitraryTolerances = false
  EqualTolerance = true
  ExtensionAngle = 0
  FormatSpec = %.2w
  FormatSpecOverTolerance = %+.2w
  FormatSpecUnderTolerance = %+.2w
  Inverted = false
  LineAngle = 0
  LockPosition = false
  MeasureType = 1
  OverTolerance = 0
  References2D = -> [View022]
  Rotation = 0
  ScaleType = 0
  TheoreticalExact = false
  Type = 2
  UnderTolerance = 0
  X = 38.9237
  Y = 1.58866
FEATURE [TechDraw::DrawViewDimension] Dimension052
  AngleOverride = false
  Arbitrary = false
  ArbitraryTolerances = false
  EqualTolerance = true
  ExtensionAngle = 0
  FormatSpec = R%.2w
  FormatSpecOverTolerance = %+.2w
  FormatSpecUnderTolerance = %+.2w
  Inverted = false
  LineAngle = 0
  LockPosition = false
  MeasureType = 1
  OverTolerance = 0
  References2D = -> [View022]
  Rotation = 0
  ScaleType = 0
  TheoreticalExact = false
  Type = 4
  UnderTolerance = 0
  X = 16.9004
  Y = -25.3506
FEATURE [TechDraw::DrawViewPart] View023
  CoarseView = false
  Direction = (0,-1,0)
  Focus = 100
  HardHidden = false
  IsoCount = 0
  IsoHidden = false
  IsoVisible = false
  LockPosition = false
  Perspective = false
  Rotation = 0
  ScaleType = 0
  SeamHidden = false
  SeamVisible = true
  SmoothHidden = false
  SmoothVisible = true
  X = 54.25
  XDirection = (1,0,0)
  XSource = -> [Link006]
  Y = 105
  expr: X = Template.Width / 4 - 20 mm
  expr: Y = Template.Height / 2
FEATURE [TechDraw::DrawViewDimension] Dimension044
  AngleOverride = false
  Arbitrary = false
  ArbitraryTolerances = false
  EqualTolerance = true
  ExtensionAngle = 0
  FormatSpec = %.2w
  FormatSpecOverTolerance = %+.2w
  FormatSpecUnderTolerance = %+.2w
  Inverted = false
  LineAngle = 0
  LockPosition = false
  MeasureType = 1
  OverTolerance = 0
  References2D = -> [View023]
  Rotation = 0
  ScaleType = 0
  TheoreticalExact = false
  Type = 1
  UnderTolerance = 0
  X = 1.36257
  Y = -55.1696
FEATURE [TechDraw::DrawViewDimension] Dimension045
  AngleOverride = false
  Arbitrary = false
  ArbitraryTolerances = false
  EqualTolerance = true
  ExtensionAngle = 0
  FormatSpec = %.2w
  FormatSpecOverTolerance = %+.2w
  FormatSpecUnderTolerance = %+.2w
  Inverted = false
  LineAngle = 0
  LockPosition = false
  MeasureType = 1
  OverTolerance = 0
  References2D = -> [View023]
  Rotation = 0
  ScaleType = 0
  TheoreticalExact = false
  Type = 2
  UnderTolerance = 0
  X = -42.7125
  Y = 1.36359
FEATURE [TechDraw::DrawViewPart] View021
  CoarseView = false
  Direction = (0,0,1)
  Focus = 100
  HardHidden = false
  IsoCount = 0
  IsoHidden = false
  IsoVisible = false
  LockPosition = false
  Perspective = false
  Rotation = 0
  ScaleType = 0
  SeamHidden = false
  SeamVisible = true
  SmoothHidden = false
  SmoothVisible = true
  X = 148.5
  XDirection = (1,0,0)
  XSource = -> [Link006]
  Y = 105
  expr: X = Template.Width / 2
  expr: Y = Template.Height / 2
FEATURE [TechDraw::DrawViewDimension] Dimension049
  AngleOverride = false
  Arbitrary = false
  ArbitraryTolerances = false
  EqualTolerance = true
  ExtensionAngle = 0
  FormatSpec = %.2w
  FormatSpecOverTolerance = %+.2w
  FormatSpecUnderTolerance = %+.2w
  Inverted = false
  LineAngle = 0
  LockPosition = false
  MeasureType = 1
  OverTolerance = 0
  References2D = -> [View021]
  Rotation = 0
  ScaleType = 0
  TheoreticalExact = false
  Type = 2
  UnderTolerance = 0
  X = -44.8736
  Y = 2.1729
FEATURE [TechDraw::DrawViewDimension] Dimension048
  AngleOverride = false
  Arbitrary = false
  ArbitraryTolerances = false
  EqualTolerance = true
  ExtensionAngle = 0
  FormatSpec = %.2w
  FormatSpecOverTolerance = %+.2w
  FormatSpecUnderTolerance = %+.2w
  Inverted = false
  LineAngle = 0
  LockPosition = false
  MeasureType = 1
  OverTolerance = 0
  References2D = -> [View021]
  Rotation = 0
  ScaleType = 0
  TheoreticalExact = false
  Type = 1
  UnderTolerance = 0
  X = 0
  Y = 51.3322
FEATURE [TechDraw::DrawViewDimension] Dimension047
  AngleOverride = false
  Arbitrary = false
  ArbitraryTolerances = false
  EqualTolerance = true
  ExtensionAngle = 0
  FormatSpec = %.2w
  FormatSpecOverTolerance = %+.2w
  FormatSpecUnderTolerance = %+.2w
  Inverted = false
  LineAngle = 0
  LockPosition = false
  MeasureType = 1
  OverTolerance = 0
  References2D = -> [View021]
  Rotation = 0
  ScaleType = 0
  TheoreticalExact = false
  Type = 2
  UnderTolerance = 0
  X = 40.2624
  Y = 25.2665
FEATURE [TechDraw::DrawViewDimension] Dimension046
  AngleOverride = false
  Arbitrary = false
  ArbitraryTolerances = false
  EqualTolerance = true
  ExtensionAngle = 0
  FormatSpec = %.2w
  FormatSpecOverTolerance = %+.2w
  FormatSpecUnderTolerance = %+.2w
  Inverted = false
  LineAngle = 0
  LockPosition = false
  MeasureType = 1
  OverTolerance = 0
  References2D = -> [View021]
  Rotation = 0
  ScaleType = 0
  TheoreticalExact = false
  Type = 1
  UnderTolerance = 0
  X = 0
  Y = -37.6133
FEATURE [TechDraw::DrawViewDimension] Dimension051
  AngleOverride = false
  Arbitrary = false
  ArbitraryTolerances = false
  EqualTolerance = true
  ExtensionAngle = 0
  FormatSpec = R%.2w
  FormatSpecOverTolerance = %+.2w
  FormatSpecUnderTolerance = %+.2w
  Inverted = false
  LineAngle = 0
  LockPosition = false
  MeasureType = 1
  OverTolerance = 0
  References2D = -> [View021]
  Rotation = 0
  ScaleType = 0
  TheoreticalExact = false
  Type = 4
  UnderTolerance = 0
  X = -22.7811
  Y = 29.5464
FEATURE [TechDraw::DrawViewDimension] Dimension050
  AngleOverride = false
  Arbitrary = false
  ArbitraryTolerances = false
  EqualTolerance = true
  ExtensionAngle = 0
  FormatSpec = R%.2w
  FormatSpecOverTolerance = %+.2w
  FormatSpecUnderTolerance = %+.2w
  Inverted = false
  LineAngle = 0
  LockPosition = false
  MeasureType = 1
  OverTolerance = 0
  References2D = -> [View021]
  Rotation = 0
  ScaleType = 0
  TheoreticalExact = false
  Type = 4
  UnderTolerance = 0
  X = 23.8856
  Y = 28.5799
FEATURE [TechDraw::DrawViewPart] View026
  CoarseView = false
  Direction = (0,0,1)
  Focus = 100
  HardHidden = false
  IsoCount = 0
  IsoHidden = false
  IsoVisible = false
  LockPosition = false
  Perspective = false
  Rotation = 0
  ScaleType = 0
  SeamHidden = false
  SeamVisible = true
  SmoothHidden = false
  SmoothVisible = true
  X = 99
  XDirection = (-0.96913,0.00479006,0.246506)
  XSource = -> [Link007]
  Y = 105
  expr: X = Template.Width / 3
FEATURE [TechDraw::DrawViewPart] View027
  CoarseView = false
  Direction = (0,1,0)
  Focus = 100
  HardHidden = false
  IsoCount = 0
  IsoHidden = false
  IsoVisible = false
  LockPosition = false
  Perspective = false
  Rotation = 0
  ScaleType = 0
  SeamHidden = false
  SeamVisible = true
  SmoothHidden = false
  SmoothVisible = true
  X = 198
  XDirection = (-1,0,0)
  XSource = -> [Link007]
  Y = 105
  expr: X = Template.Width / 3 * 2
FEATURE [TechDraw::DrawViewPart] View028
  CoarseView = false
  Direction = (0,0,1)
  Focus = 100
  HardHidden = false
  IsoCount = 0
  IsoHidden = false
  IsoVisible = false
  LockPosition = false
  Perspective = false
  Rotation = 0
  ScaleType = 0
  SeamHidden = false
  SeamVisible = true
  SmoothHidden = false
  SmoothVisible = true
  X = 99
  XDirection = (-0.96913,0.00479006,0.246506)
  XSource = -> [Link008]
  Y = 105
  expr: X = Template.Width / 3
FEATURE [TechDraw::DrawViewPart] View029
  CoarseView = false
  Direction = (0,1,0)
  Focus = 100
  HardHidden = false
  IsoCount = 0
  IsoHidden = false
  IsoVisible = false
  LockPosition = false
  Perspective = false
  Rotation = 0
  ScaleType = 0
  SeamHidden = false
  SeamVisible = true
  SmoothHidden = false
  SmoothVisible = true
  X = 198
  XDirection = (-1,0,0)
  XSource = -> [Link008]
  Y = 105
  expr: X = Template.Width / 3 * 2
FEATURE [TechDraw::DrawViewDimension] Dimension062
  AngleOverride = false
  Arbitrary = false
  ArbitraryTolerances = false
  EqualTolerance = true
  ExtensionAngle = 0
  FormatSpec = %.2w
  FormatSpecOverTolerance = %+.2w
  FormatSpecUnderTolerance = %+.2w
  Inverted = false
  LineAngle = 0
  LockPosition = false
  MeasureType = 1
  OverTolerance = 0
  References2D = -> [View026]
  Rotation = 0
  ScaleType = 0
  TheoreticalExact = false
  Type = 1
  UnderTolerance = 0
  X = -0.488527
  Y = -29.443
FEATURE [TechDraw::DrawViewDimension] Dimension063
  AngleOverride = false
  Arbitrary = false
  ArbitraryTolerances = false
  EqualTolerance = true
  ExtensionAngle = 0
  FormatSpec = %.2w
  FormatSpecOverTolerance = %+.2w
  FormatSpecUnderTolerance = %+.2w
  Inverted = false
  LineAngle = 0
  LockPosition = false
  MeasureType = 1
  OverTolerance = 0
  References2D = -> [View026]
  Rotation = 0
  ScaleType = 0
  TheoreticalExact = false
  Type = 2
  UnderTolerance = 0
  X = -53.4412
  Y = 5.44583
FEATURE [TechDraw::DrawViewDimension] Dimension064
  AngleOverride = false
  Arbitrary = false
  ArbitraryTolerances = false
  EqualTolerance = true
  ExtensionAngle = 0
  FormatSpec = %.2w
  FormatSpecOverTolerance = %+.2w
  FormatSpecUnderTolerance = %+.2w
  Inverted = false
  LineAngle = 0
  LockPosition = false
  MeasureType = 1
  OverTolerance = 0
  References2D = -> [View027]
  Rotation = 0
  ScaleType = 0
  TheoreticalExact = false
  Type = 2
  UnderTolerance = 0
  X = -45.1531
  Y = -0.401318
FEATURE [TechDraw::DrawViewDimension] Dimension065
  AngleOverride = false
  Arbitrary = false
  ArbitraryTolerances = false
  EqualTolerance = true
  ExtensionAngle = 0
  FormatSpec = %.2w
  FormatSpecOverTolerance = %+.2w
  FormatSpecUnderTolerance = %+.2w
  Inverted = false
  LineAngle = 0
  LockPosition = false
  MeasureType = 1
  OverTolerance = 0
  References2D = -> [View027]
  Rotation = 0
  ScaleType = 0
  TheoreticalExact = false
  Type = 2
  UnderTolerance = 0
  X = 40.0885
  Y = 5.09558
FEATURE [TechDraw::DrawViewDimension] Dimension066
  AngleOverride = false
  Arbitrary = false
  ArbitraryTolerances = false
  EqualTolerance = true
  ExtensionAngle = 0
  FormatSpec = %.2w
  FormatSpecOverTolerance = %+.2w
  FormatSpecUnderTolerance = %+.2w
  Inverted = false
  LineAngle = 0
  LockPosition = false
  MeasureType = 1
  OverTolerance = 0
  References2D = -> [View028]
  Rotation = 0
  ScaleType = 0
  TheoreticalExact = false
  Type = 1
  UnderTolerance = 0
  X = 0.955139
  Y = -19.88
FEATURE [TechDraw::DrawViewDimension] Dimension067
  AngleOverride = false
  Arbitrary = false
  ArbitraryTolerances = false
  EqualTolerance = true
  ExtensionAngle = 0
  FormatSpec = %.2w
  FormatSpecOverTolerance = %+.2w
  FormatSpecUnderTolerance = %+.2w
  Inverted = false
  LineAngle = 0
  LockPosition = false
  MeasureType = 1
  OverTolerance = 0
  References2D = -> [View028]
  Rotation = 0
  ScaleType = 0
  TheoreticalExact = false
  Type = 2
  UnderTolerance = 0
  X = 41.3952
  Y = 4.31736
FEATURE [TechDraw::DrawViewDimension] Dimension068
  AngleOverride = false
  Arbitrary = false
  ArbitraryTolerances = false
  EqualTolerance = true
  ExtensionAngle = 0
  FormatSpec = %.2w
  FormatSpecOverTolerance = %+.2w
  FormatSpecUnderTolerance = %+.2w
  Inverted = false
  LineAngle = 0
  LockPosition = false
  MeasureType = 1
  OverTolerance = 0
  References2D = -> [View029]
  Rotation = 0
  ScaleType = 0
  TheoreticalExact = false
  Type = 2
  UnderTolerance = 0
  X = 51.2853
  Y = 2.70931
FEATURE [TechDraw::DrawViewDimension] Dimension069
  AngleOverride = false
  Arbitrary = false
  ArbitraryTolerances = false
  EqualTolerance = true
  ExtensionAngle = 0
  FormatSpec = %.2w
  FormatSpecOverTolerance = %+.2w
  FormatSpecUnderTolerance = %+.2w
  Inverted = false
  LineAngle = 0
  LockPosition = false
  MeasureType = 1
  OverTolerance = 0
  References2D = -> [View029]
  Rotation = 0
  ScaleType = 0
  TheoreticalExact = false
  Type = 2
  UnderTolerance = 0
  X = -43.3334
  Y = 4.21295
FEATURE [TechDraw::DrawViewDimension] Dimension070
  AngleOverride = false
  Arbitrary = false
  ArbitraryTolerances = false
  EqualTolerance = true
  ExtensionAngle = 0
  FormatSpec = %.2w
  FormatSpecOverTolerance = %+.2w
  FormatSpecUnderTolerance = %+.2w
  Inverted = false
  LineAngle = 0
  LockPosition = false
  MeasureType = 1
  OverTolerance = 0
  References2D = -> [View029]
  Rotation = 0
  ScaleType = 0
  TheoreticalExact = false
  Type = 1
  UnderTolerance = 0
  X = 0
  Y = 65.8241
FEATURE [Part::Feature] Unfold009  label="dec_corner_unfold"
  shape: bbox 55.63 x 0.5612 x 1123 mm, 19 faces (baked)
FEATURE [Sketcher::SketchObject] Unfold_Sketch009  label="dec_corner_Sketch"
  FullyConstrained = false
  sketch-geometry (17):
    g0: LineSegment StartX=5 StartY=37.3343 StartZ=0 EndX=1118 EndY=37.3343 EndZ=0
    g1: BSplineCurve PolesCount=22 KnotsCount=5 Degree=6 IsPeriodic=0
    g2: BSplineCurve PolesCount=22 KnotsCount=5 Degree=6 IsPeriodic=0
    g3: LineSegment StartX=0 StartY=-13.3 StartZ=0 EndX=0 EndY=32.3343 EndZ=0
    g4: BSplineCurve PolesCount=22 KnotsCount=5 Degree=6 IsPeriodic=0
    g5: LineSegment StartX=5 StartY=-18.3 StartZ=0 EndX=1118 EndY=-18.3 EndZ=0
    g6: BSplineCurve PolesCount=22 KnotsCount=5 Degree=6 IsPeriodic=0
    g7: LineSegment StartX=1123 StartY=-13.3 StartZ=0 EndX=1123 EndY=32.3343 EndZ=0
    g8: Circle CenterX=123 CenterY=31.3343 CenterZ=0 NormalX=0 NormalY=0 NormalZ=-1 AngleXU=-1.5708 Radius=1.7
    g9: Circle CenterX=963 CenterY=31.3343 CenterZ=0 NormalX=0 NormalY=0 NormalZ=-1 AngleXU=-1.5708 Radius=1.7
    g10: Circle CenterX=543 CenterY=31.3343 CenterZ=0 NormalX=0 NormalY=0 NormalZ=-1 AngleXU=-1.5708 Radius=1.7
    g11: Circle CenterX=1015 CenterY=0 CenterZ=0 NormalX=0 NormalY=0 NormalZ=1 AngleXU=-1.5708 Radius=1.7
    g12: Circle CenterX=815 CenterY=0 CenterZ=0 NormalX=0 NormalY=0 NormalZ=1 AngleXU=-1.5708 Radius=1.7
    g13: Circle CenterX=615 CenterY=0 CenterZ=0 NormalX=0 NormalY=0 NormalZ=1 AngleXU=-1.5708 Radius=1.7
    g14: Circle CenterX=15 CenterY=0 CenterZ=0 NormalX=0 NormalY=0 NormalZ=1 AngleXU=-1.5708 Radius=1.7
    g15: Circle CenterX=415 CenterY=0 CenterZ=0 NormalX=0 NormalY=0 NormalZ=1 AngleXU=-1.5708 Radius=1.7
    g16: Circle CenterX=215 CenterY=0 CenterZ=0 NormalX=0 NormalY=0 NormalZ=1 AngleXU=-1.5708 Radius=1.7
FEATURE [Sketcher::SketchObject] Unfold_Sketch_bends009  label="dec_corner_bends"
  FullyConstrained = false
  Placement = pos=(0,15.5015,6.30649) rot=(-1,0,0;1.18441rad)
  sketch-geometry (1):
    g0: LineSegment StartX=1123 StartY=6.80841 StartZ=0 EndX=0 EndY=6.80841 EndZ=0
FEATURE [TechDraw::DrawSVGTemplate] Template
  Height = 210
  Orientation = 1
  Template = <path>
  Width = 297
FEATURE [TechDraw::DrawPage] Page
  KeepUpdated = true
  NextBalloonIndex = 1
  ProjectionType = 0
  Template = -> Template
  Views = -> [View,View002,Dimension,Dimension001,Dimension003,Dimension004,View003,Dimension005,Dimension006,Dimension007,Dimension027]
FEATURE [App::DocumentObjectGroup] Group  label="cover"
  Group = -> [Link004,Unfold002,Unfold_Sketch002,Unfold_Sketch_Outline002,Unfold_Sketch_Internal001,Unfold_Sketch_bends002,Page]
FEATURE [TechDraw::DrawPage] Page001
  KeepUpdated = true
  NextBalloonIndex = 1
  ProjectionType = 0
  Template = -> Template
  Views = -> [View004,View005,View006,Dimension008,Dimension009,Dimension010,Dimension011,Dimension012,Dimension013,Dimension014,Dimension015,Dimension016]
FEATURE [App::DocumentObjectGroup] Group001  label="pillar001"
  Group = -> [Link,Page001,Unfold004,Unfold_Sketch004,Unfold_Sketch_Outline004,Unfold_Sketch_Internal003,Unfold_Sketch_bends004]
FEATURE [TechDraw::DrawPage] Page002
  KeepUpdated = true
  NextBalloonIndex = 1
  ProjectionType = 0
  Template = -> Template
  Views = -> [View007,View008,View009,Dimension021,Dimension022,Dimension040,Dimension041]
FEATURE [TechDraw::DrawPage] Page003
  KeepUpdated = true
  NextBalloonIndex = 1
  ProjectionType = 0
  Template = -> Template
  Views = -> [View010,View011,View012,Dimension023,Dimension024,Dimension025,Dimension026]
FEATURE [App::DocumentObjectGroup] Group003  label="pillar_top"
  Group = -> [Unfold001,Unfold_Sketch001,Unfold_Sketch_Outline001,Unfold_Sketch_Internal,Unfold_Sketch_bends001,Link001,Page003]
FEATURE [TechDraw::DrawPage] Page005
  KeepUpdated = true
  NextBalloonIndex = 1
  ProjectionType = 0
  Template = -> Template
  Views = -> [View016,View017,Dimension033,Dimension042,Dimension043]
FEATURE [App::DocumentObjectGroup] Group002  label="pillar_bottom"
  Group = -> [Link002,Page002,Part__Mirroring,Page005,Unfold,Unfold_Sketch,Unfold_Sketch_bends,Part__Mirroring003,MirroredSketch,MirroredSketch002]
FEATURE [TechDraw::DrawPage] Page006
  KeepUpdated = true
  NextBalloonIndex = 1
  ProjectionType = 0
  Template = -> Template
  Views = -> [View018,View019,View020,Dimension036,Dimension037,Dimension038,Dimension039]
FEATURE [TechDraw::DrawPage] Page007
  KeepUpdated = true
  NextBalloonIndex = 1
  ProjectionType = 0
  Template = -> Template
  Views = -> [View018,View019,View020,Dimension036,Dimension037,Dimension038,Dimension039]
  expr: Views = Page006.Views
FEATURE [TechDraw::DrawPage] Page008
  KeepUpdated = true
  NextBalloonIndex = 1
  ProjectionType = 0
  Template = -> Template
  Views = -> [View024,View025,Dimension055,Dimension056,Dimension057,Dimension058,Dimension059,Dimension060,Dimension061]
FEATURE [App::DocumentObjectGroup] Group006  label="pillar2"
  Group = -> [Link005,Unfold006,Unfold_Sketch006,Unfold_Sketch_bends006,Body,Page008]
FEATURE [TechDraw::DrawPage] Page009
  KeepUpdated = true
  NextBalloonIndex = 1
  ProjectionType = 0
  Template = -> Template
  Views = -> [View021,View022,View023,Dimension044,Dimension045,Dimension046,Dimension047,Dimension048,Dimension049,Dimension050,Dimension051,Dimension052,Dimension053,Dimension054]
FEATURE [App::DocumentObjectGroup] Group007  label="pillar_top_element"
  Group = -> [Link006,Unfold_Sketch_bends005,Unfold005,Unfold_Sketch005,Page009]
FEATURE [TechDraw::DrawPage] Page010  label="top_dec_corner_mirror_page"
  KeepUpdated = true
  NextBalloonIndex = 1
  ProjectionType = 0
  Template = -> Template
  Views = -> [View026,View027,Dimension062,Dimension063,Dimension064,Dimension065]
FEATURE [TechDraw::DrawPage] Page011  label="top_dec_corner_page"
  KeepUpdated = true
  NextBalloonIndex = 1
  ProjectionType = 0
  Template = -> Template
  Views = -> [View028,View029,Dimension066,Dimension067,Dimension068,Dimension069,Dimension070]
FEATURE [App::DocumentObjectGroup] Group008  label="top_dec_corner"
  Group = -> [Link007,Link008,Unfold_Sketch_bends007,Unfold007,Unfold_Sketch007,Unfold_Sketch_bends008,Unfold008,Unfold_Sketch008,Page011,Page010]
FEATURE [Sketcher::SketchObject] MirroredSketch003  label="dec_corner_mirror_sketch"
  FullyConstrained = false
  sketch-geometry (17):
    g0: LineSegment StartX=5 StartY=-37.3343 StartZ=0 EndX=1118 EndY=-37.3343 EndZ=0
    g1: BSplineCurve PolesCount=22 KnotsCount=5 Degree=6 IsPeriodic=0
    g2: BSplineCurve PolesCount=22 KnotsCount=5 Degree=6 IsPeriodic=0
    g3: LineSegment StartX=0 StartY=13.3 StartZ=0 EndX=0 EndY=-32.3343 EndZ=0
    g4: BSplineCurve PolesCount=22 KnotsCount=5 Degree=6 IsPeriodic=0
    g5: LineSegment StartX=5 StartY=18.3 StartZ=0 EndX=1118 EndY=18.3 EndZ=0
    g6: BSplineCurve PolesCount=22 KnotsCount=5 Degree=6 IsPeriodic=0
    g7: LineSegment StartX=1123 StartY=13.3 StartZ=0 EndX=1123 EndY=-32.3343 EndZ=0
    g8: Circle CenterX=123 CenterY=-31.3343 CenterZ=0 NormalX=0 NormalY=0 NormalZ=-1 AngleXU=-1.5708 Radius=1.7
    g9: Circle CenterX=963 CenterY=-31.3343 CenterZ=0 NormalX=0 NormalY=0 NormalZ=-1 AngleXU=-1.5708 Radius=1.7
    g10: Circle CenterX=543 CenterY=-31.3343 CenterZ=0 NormalX=0 NormalY=0 NormalZ=-1 AngleXU=-1.5708 Radius=1.7
    g11: Circle CenterX=1015 CenterY=0 CenterZ=0 NormalX=0 NormalY=0 NormalZ=1 AngleXU=-1.5708 Radius=1.7
    g12: Circle CenterX=815 CenterY=0 CenterZ=0 NormalX=0 NormalY=0 NormalZ=1 AngleXU=-1.5708 Radius=1.7
    g13: Circle CenterX=615 CenterY=0 CenterZ=0 NormalX=0 NormalY=0 NormalZ=1 AngleXU=-1.5708 Radius=1.7
    g14: Circle CenterX=15 CenterY=0 CenterZ=0 NormalX=0 NormalY=0 NormalZ=1 AngleXU=-1.5708 Radius=1.7
    g15: Circle CenterX=415 CenterY=0 CenterZ=0 NormalX=0 NormalY=0 NormalZ=1 AngleXU=-1.5708 Radius=1.7
    g16: Circle CenterX=215 CenterY=0 CenterZ=0 NormalX=0 NormalY=0 NormalZ=1 AngleXU=-1.5708 Radius=1.7
FEATURE [App::DocumentObjectGroup] Group005  label="dec_corner"
  Group = -> [Link003,Page006,Part__Mirroring001,Page007,Unfold009,Unfold_Sketch009,Unfold_Sketch_bends009,MirroredSketch003]
note: 1 file-system path scrubbed to <path> (originals preserved in the JSON sidecar)
